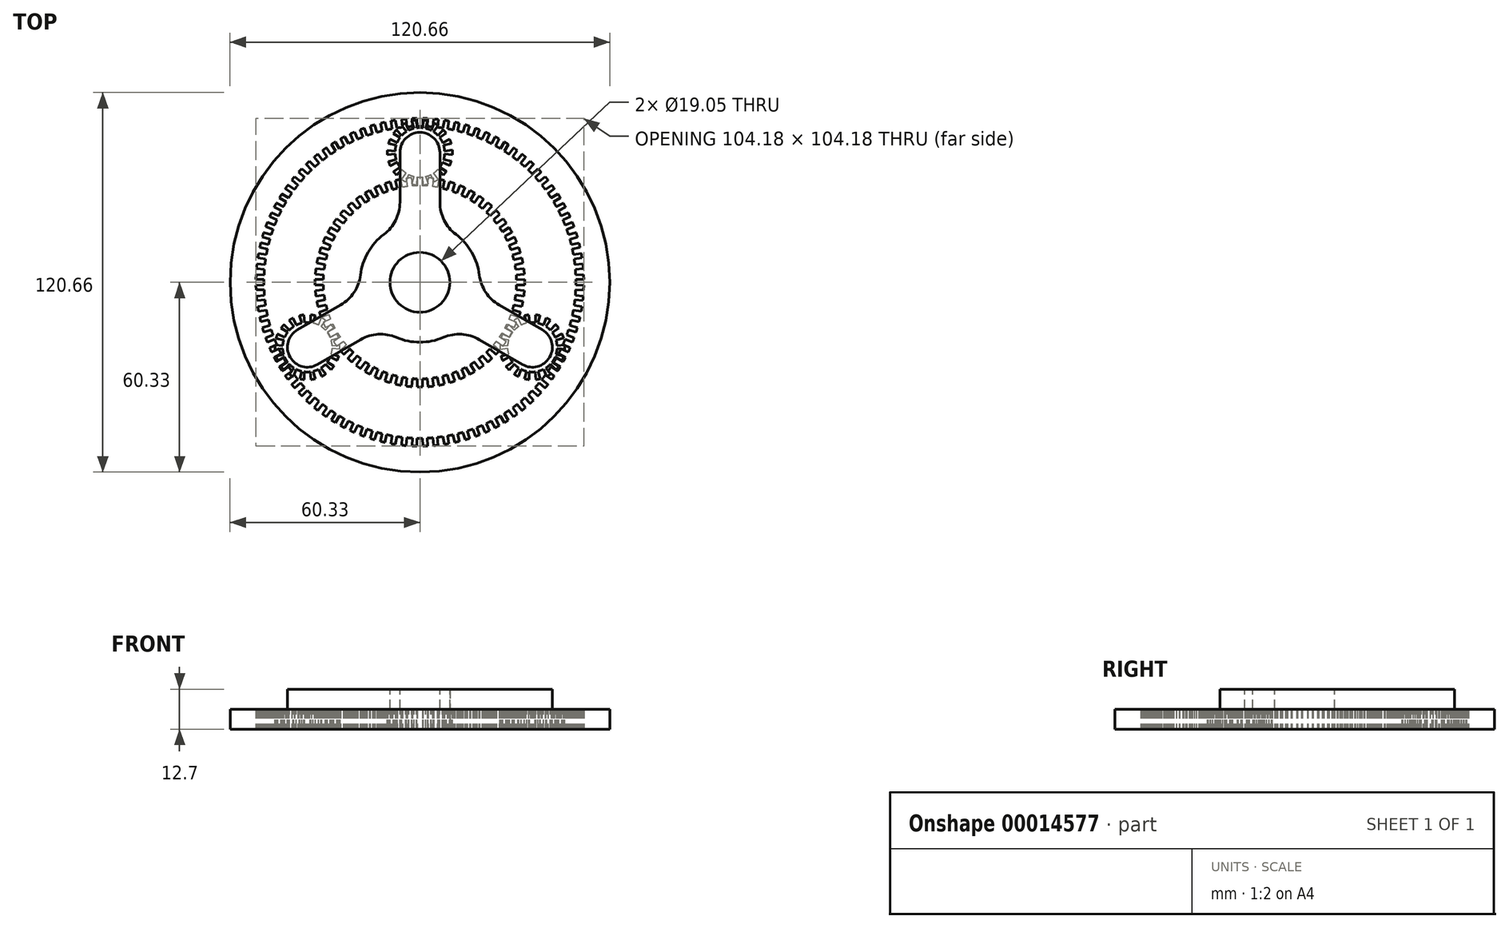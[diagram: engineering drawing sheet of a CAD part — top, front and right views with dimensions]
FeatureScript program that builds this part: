
annotation { "Feature Type Name" : "Feature", "Feature Type Description" : "" }
export const myFeature = defineFeature(function(context is Context, id is Id, definition is map)
    precondition{}
    {
        {
            var Q0;
            Q0=qCreatedBy(makeId("Top.planeOp"),FACE);
            var sketch = newSketch(context, id + "F0", { "sketchPlane" : qUnion([Q0])});
            skCircle(sketch, "E0", {"center": v(0, 0) * mm, "radius": 9.53 * mm});
            skCircle(sketch, "E1", {"center": v(0, 0) * mm, "radius": 31.75 * mm, "construction": true});
            skLineSegment(sketch, "E2", {"start": v(0.87, 30.7) * mm, "end": v(0.87, 33.3) * mm});
            skArc(sketch, "E3", {"start": v(0.87, 33.3) * mm, "mid": v(0, 33.3) * mm, "end": v(-0.87, 33.3) * mm});
            skLineSegment(sketch, "E4", {"start": v(-0.87, 33.3) * mm, "end": v(-0.83, 30.7) * mm});
            skArc(sketch, "E5", {"start": v(-0.83, 30.7) * mm, "mid": v(-1.59, 30.66) * mm, "end": v(-2.34, 30.61) * mm});
            skLineSegment(sketch, "E6", {"start": v(1.05, 36.8) * mm, "end": v(0, 0) * mm, "construction": true});
            skLineSegment(sketch, "E7", {"start": v(0, 0) * mm, "end": v(-2.79, 36.45) * mm, "construction": true});
            skLineSegment(sketch, "E8.1.0", {"start": v(-2.34, 30.61) * mm, "end": v(-2.61, 33.2) * mm});
            skArc(sketch, "E8.1.1", {"start": v(-2.61, 33.2) * mm, "mid": v(-3.48, 33.13) * mm, "end": v(-4.35, 33.02) * mm});
            skLineSegment(sketch, "E8.1.2", {"start": v(-4.35, 33.02) * mm, "end": v(-4.04, 30.44) * mm});
            skArc(sketch, "E8.1.3", {"start": v(-4.04, 30.44) * mm, "mid": v(-4.78, 30.33) * mm, "end": v(-5.53, 30.2) * mm});
            skLineSegment(sketch, "E8.2.0", {"start": v(-5.53, 30.2) * mm, "end": v(-6.07, 32.75) * mm});
            skArc(sketch, "E8.2.1", {"start": v(-6.07, 32.75) * mm, "mid": v(-6.93, 32.58) * mm, "end": v(-7.78, 32.39) * mm});
            skLineSegment(sketch, "E8.2.2", {"start": v(-7.78, 32.39) * mm, "end": v(-7.2, 29.85) * mm});
            skArc(sketch, "E8.2.3", {"start": v(-7.2, 29.85) * mm, "mid": v(-7.93, 29.66) * mm, "end": v(-8.65, 29.46) * mm});
            skLineSegment(sketch, "E8.3.0", {"start": v(-8.65, 29.46) * mm, "end": v(-9.46, 31.94) * mm});
            skArc(sketch, "E8.3.1", {"start": v(-9.46, 31.94) * mm, "mid": v(-10.3, 31.68) * mm, "end": v(-11.12, 31.4) * mm});
            skLineSegment(sketch, "E8.3.2", {"start": v(-11.12, 31.4) * mm, "end": v(-10.28, 28.93) * mm});
            skArc(sketch, "E8.3.3", {"start": v(-10.28, 28.93) * mm, "mid": v(-10.98, 28.67) * mm, "end": v(-11.69, 28.4) * mm});
            skLineSegment(sketch, "E8.4.0", {"start": v(-11.69, 28.4) * mm, "end": v(-12.75, 30.77) * mm});
            skArc(sketch, "E8.4.1", {"start": v(-12.75, 30.77) * mm, "mid": v(-13.55, 30.43) * mm, "end": v(-14.34, 30.06) * mm});
            skLineSegment(sketch, "E8.4.2", {"start": v(-14.34, 30.06) * mm, "end": v(-13.24, 27.7) * mm});
            skArc(sketch, "E8.4.3", {"start": v(-13.24, 27.7) * mm, "mid": v(-13.92, 27.37) * mm, "end": v(-14.59, 27.01) * mm});
            skLineSegment(sketch, "E8.5.0", {"start": v(-14.59, 27.01) * mm, "end": v(-15.9, 29.27) * mm});
            skArc(sketch, "E8.5.1", {"start": v(-15.9, 29.27) * mm, "mid": v(-16.65, 28.85) * mm, "end": v(-17.4, 28.4) * mm});
            skLineSegment(sketch, "E8.5.2", {"start": v(-17.4, 28.4) * mm, "end": v(-16.07, 26.16) * mm});
            skArc(sketch, "E8.5.3", {"start": v(-16.07, 26.16) * mm, "mid": v(-16.7, 25.76) * mm, "end": v(-17.33, 25.34) * mm});
            skLineSegment(sketch, "E8.6.0", {"start": v(-17.33, 25.34) * mm, "end": v(-18.87, 27.45) * mm});
            skArc(sketch, "E8.6.1", {"start": v(-18.87, 27.45) * mm, "mid": v(-19.58, 26.95) * mm, "end": v(-20.28, 26.42) * mm});
            skLineSegment(sketch, "E8.6.2", {"start": v(-20.28, 26.42) * mm, "end": v(-18.71, 24.34) * mm});
            skArc(sketch, "E8.6.3", {"start": v(-18.71, 24.34) * mm, "mid": v(-19.3, 23.87) * mm, "end": v(-19.89, 23.4) * mm});
            skLineSegment(sketch, "E8.7.0", {"start": v(-19.89, 23.4) * mm, "end": v(-21.63, 25.33) * mm});
            skArc(sketch, "E8.7.1", {"start": v(-21.63, 25.33) * mm, "mid": v(-22.29, 24.75) * mm, "end": v(-22.93, 24.16) * mm});
            skLineSegment(sketch, "E8.7.2", {"start": v(-22.93, 24.16) * mm, "end": v(-21.16, 22.25) * mm});
            skArc(sketch, "E8.7.3", {"start": v(-21.16, 22.25) * mm, "mid": v(-21.7, 21.72) * mm, "end": v(-22.22, 21.18) * mm});
            skLineSegment(sketch, "E8.8.0", {"start": v(-22.22, 21.18) * mm, "end": v(-24.16, 22.93) * mm});
            skArc(sketch, "E8.8.1", {"start": v(-24.16, 22.93) * mm, "mid": v(-24.75, 22.29) * mm, "end": v(-25.33, 21.63) * mm});
            skLineSegment(sketch, "E8.8.2", {"start": v(-25.33, 21.63) * mm, "end": v(-23.37, 19.92) * mm});
            skArc(sketch, "E8.8.3", {"start": v(-23.37, 19.92) * mm, "mid": v(-23.85, 19.34) * mm, "end": v(-24.32, 18.75) * mm});
            skLineSegment(sketch, "E8.9.0", {"start": v(-24.32, 18.75) * mm, "end": v(-26.42, 20.28) * mm});
            skArc(sketch, "E8.9.1", {"start": v(-26.42, 20.28) * mm, "mid": v(-26.95, 19.58) * mm, "end": v(-27.45, 18.87) * mm});
            skLineSegment(sketch, "E8.9.2", {"start": v(-27.45, 18.87) * mm, "end": v(-25.32, 17.37) * mm});
            skArc(sketch, "E8.9.3", {"start": v(-25.32, 17.37) * mm, "mid": v(-25.74, 16.74) * mm, "end": v(-26.14, 16.1) * mm});
            skLineSegment(sketch, "E8.10.0", {"start": v(-26.14, 16.1) * mm, "end": v(-28.4, 17.4) * mm});
            skArc(sketch, "E8.10.1", {"start": v(-28.4, 17.4) * mm, "mid": v(-28.85, 16.65) * mm, "end": v(-29.27, 15.9) * mm});
            skLineSegment(sketch, "E8.10.2", {"start": v(-29.27, 15.9) * mm, "end": v(-27, 14.62) * mm});
            skArc(sketch, "E8.10.3", {"start": v(-27, 14.62) * mm, "mid": v(-27.35, 13.96) * mm, "end": v(-27.68, 13.28) * mm});
            skLineSegment(sketch, "E8.11.0", {"start": v(-27.68, 13.28) * mm, "end": v(-30.06, 14.34) * mm});
            skArc(sketch, "E8.11.1", {"start": v(-30.06, 14.34) * mm, "mid": v(-30.43, 13.55) * mm, "end": v(-30.77, 12.75) * mm});
            skLineSegment(sketch, "E8.11.2", {"start": v(-30.77, 12.75) * mm, "end": v(-28.38, 11.72) * mm});
            skArc(sketch, "E8.11.3", {"start": v(-28.38, 11.72) * mm, "mid": v(-28.66, 11.02) * mm, "end": v(-28.92, 10.31) * mm});
            skLineSegment(sketch, "E8.12.0", {"start": v(-28.92, 10.31) * mm, "end": v(-31.4, 11.12) * mm});
            skArc(sketch, "E8.12.1", {"start": v(-31.4, 11.12) * mm, "mid": v(-31.68, 10.3) * mm, "end": v(-31.94, 9.46) * mm});
            skLineSegment(sketch, "E8.12.2", {"start": v(-31.94, 9.46) * mm, "end": v(-29.45, 8.7) * mm});
            skArc(sketch, "E8.12.3", {"start": v(-29.45, 8.7) * mm, "mid": v(-29.65, 7.97) * mm, "end": v(-29.84, 7.23) * mm});
            skLineSegment(sketch, "E8.13.0", {"start": v(-29.84, 7.23) * mm, "end": v(-32.39, 7.78) * mm});
            skArc(sketch, "E8.13.1", {"start": v(-32.39, 7.78) * mm, "mid": v(-32.58, 6.93) * mm, "end": v(-32.75, 6.07) * mm});
            skLineSegment(sketch, "E8.13.2", {"start": v(-32.75, 6.07) * mm, "end": v(-30.2, 5.57) * mm});
            skArc(sketch, "E8.13.3", {"start": v(-30.2, 5.57) * mm, "mid": v(-30.32, 4.82) * mm, "end": v(-30.43, 4.08) * mm});
            skLineSegment(sketch, "E8.14.0", {"start": v(-30.43, 4.08) * mm, "end": v(-33.02, 4.35) * mm});
            skArc(sketch, "E8.14.1", {"start": v(-33.02, 4.35) * mm, "mid": v(-33.13, 3.48) * mm, "end": v(-33.2, 2.61) * mm});
            skLineSegment(sketch, "E8.14.2", {"start": v(-33.2, 2.61) * mm, "end": v(-30.61, 2.38) * mm});
            skArc(sketch, "E8.14.3", {"start": v(-30.61, 2.38) * mm, "mid": v(-30.66, 1.63) * mm, "end": v(-30.7, 0.87) * mm});
            skLineSegment(sketch, "E8.15.0", {"start": v(-30.7, 0.87) * mm, "end": v(-33.3, 0.87) * mm});
            skArc(sketch, "E8.15.1", {"start": v(-33.3, 0.87) * mm, "mid": v(-33.3, 0) * mm, "end": v(-33.3, -0.87) * mm});
            skLineSegment(sketch, "E8.15.2", {"start": v(-33.3, -0.87) * mm, "end": v(-30.7, -0.83) * mm});
            skArc(sketch, "E8.15.3", {"start": v(-30.7, -0.83) * mm, "mid": v(-30.66, -1.59) * mm, "end": v(-30.61, -2.34) * mm});
            skLineSegment(sketch, "E8.16.0", {"start": v(-30.61, -2.34) * mm, "end": v(-33.2, -2.61) * mm});
            skArc(sketch, "E8.16.1", {"start": v(-33.2, -2.61) * mm, "mid": v(-33.13, -3.48) * mm, "end": v(-33.02, -4.35) * mm});
            skLineSegment(sketch, "E8.16.2", {"start": v(-33.02, -4.35) * mm, "end": v(-30.44, -4.04) * mm});
            skArc(sketch, "E8.16.3", {"start": v(-30.44, -4.04) * mm, "mid": v(-30.33, -4.78) * mm, "end": v(-30.2, -5.53) * mm});
            skLineSegment(sketch, "E8.17.0", {"start": v(-30.2, -5.53) * mm, "end": v(-32.75, -6.07) * mm});
            skArc(sketch, "E8.17.1", {"start": v(-32.75, -6.07) * mm, "mid": v(-32.58, -6.93) * mm, "end": v(-32.39, -7.78) * mm});
            skLineSegment(sketch, "E8.17.2", {"start": v(-32.39, -7.78) * mm, "end": v(-29.85, -7.2) * mm});
            skArc(sketch, "E8.17.3", {"start": v(-29.85, -7.2) * mm, "mid": v(-29.66, -7.93) * mm, "end": v(-29.46, -8.65) * mm});
            skLineSegment(sketch, "E8.18.0", {"start": v(-29.46, -8.65) * mm, "end": v(-31.94, -9.46) * mm});
            skArc(sketch, "E8.18.1", {"start": v(-31.94, -9.46) * mm, "mid": v(-31.68, -10.3) * mm, "end": v(-31.4, -11.12) * mm});
            skLineSegment(sketch, "E8.18.2", {"start": v(-31.4, -11.12) * mm, "end": v(-28.93, -10.28) * mm});
            skArc(sketch, "E8.18.3", {"start": v(-28.93, -10.28) * mm, "mid": v(-28.67, -10.98) * mm, "end": v(-28.4, -11.69) * mm});
            skLineSegment(sketch, "E8.19.0", {"start": v(-28.4, -11.69) * mm, "end": v(-30.77, -12.75) * mm});
            skArc(sketch, "E8.19.1", {"start": v(-30.77, -12.75) * mm, "mid": v(-30.43, -13.55) * mm, "end": v(-30.06, -14.34) * mm});
            skLineSegment(sketch, "E8.19.2", {"start": v(-30.06, -14.34) * mm, "end": v(-27.7, -13.24) * mm});
            skArc(sketch, "E8.19.3", {"start": v(-27.7, -13.24) * mm, "mid": v(-27.37, -13.92) * mm, "end": v(-27.01, -14.59) * mm});
            skLineSegment(sketch, "E8.20.0", {"start": v(-27.01, -14.59) * mm, "end": v(-29.27, -15.9) * mm});
            skArc(sketch, "E8.20.1", {"start": v(-29.27, -15.9) * mm, "mid": v(-28.85, -16.65) * mm, "end": v(-28.4, -17.4) * mm});
            skLineSegment(sketch, "E8.20.2", {"start": v(-28.4, -17.4) * mm, "end": v(-26.16, -16.07) * mm});
            skArc(sketch, "E8.20.3", {"start": v(-26.16, -16.07) * mm, "mid": v(-25.76, -16.7) * mm, "end": v(-25.34, -17.33) * mm});
            skLineSegment(sketch, "E8.21.0", {"start": v(-25.34, -17.33) * mm, "end": v(-27.45, -18.87) * mm});
            skArc(sketch, "E8.21.1", {"start": v(-27.45, -18.87) * mm, "mid": v(-26.95, -19.58) * mm, "end": v(-26.42, -20.28) * mm});
            skLineSegment(sketch, "E8.21.2", {"start": v(-26.42, -20.28) * mm, "end": v(-24.34, -18.71) * mm});
            skArc(sketch, "E8.21.3", {"start": v(-24.34, -18.71) * mm, "mid": v(-23.87, -19.3) * mm, "end": v(-23.4, -19.89) * mm});
            skLineSegment(sketch, "E8.22.0", {"start": v(-23.4, -19.89) * mm, "end": v(-25.33, -21.63) * mm});
            skArc(sketch, "E8.22.1", {"start": v(-25.33, -21.63) * mm, "mid": v(-24.75, -22.29) * mm, "end": v(-24.16, -22.93) * mm});
            skLineSegment(sketch, "E8.22.2", {"start": v(-24.16, -22.93) * mm, "end": v(-22.25, -21.16) * mm});
            skArc(sketch, "E8.22.3", {"start": v(-22.25, -21.16) * mm, "mid": v(-21.72, -21.7) * mm, "end": v(-21.18, -22.22) * mm});
            skLineSegment(sketch, "E8.23.0", {"start": v(-21.18, -22.22) * mm, "end": v(-22.93, -24.16) * mm});
            skArc(sketch, "E8.23.1", {"start": v(-22.93, -24.16) * mm, "mid": v(-22.29, -24.75) * mm, "end": v(-21.63, -25.33) * mm});
            skLineSegment(sketch, "E8.23.2", {"start": v(-21.63, -25.33) * mm, "end": v(-19.92, -23.37) * mm});
            skArc(sketch, "E8.23.3", {"start": v(-19.92, -23.37) * mm, "mid": v(-19.34, -23.85) * mm, "end": v(-18.75, -24.32) * mm});
            skLineSegment(sketch, "E8.24.0", {"start": v(-18.75, -24.32) * mm, "end": v(-20.28, -26.42) * mm});
            skArc(sketch, "E8.24.1", {"start": v(-20.28, -26.42) * mm, "mid": v(-19.58, -26.95) * mm, "end": v(-18.87, -27.45) * mm});
            skLineSegment(sketch, "E8.24.2", {"start": v(-18.87, -27.45) * mm, "end": v(-17.37, -25.32) * mm});
            skArc(sketch, "E8.24.3", {"start": v(-17.37, -25.32) * mm, "mid": v(-16.74, -25.74) * mm, "end": v(-16.1, -26.14) * mm});
            skLineSegment(sketch, "E8.25.0", {"start": v(-16.1, -26.14) * mm, "end": v(-17.4, -28.4) * mm});
            skArc(sketch, "E8.25.1", {"start": v(-17.4, -28.4) * mm, "mid": v(-16.65, -28.85) * mm, "end": v(-15.9, -29.27) * mm});
            skLineSegment(sketch, "E8.25.2", {"start": v(-15.9, -29.27) * mm, "end": v(-14.62, -27) * mm});
            skArc(sketch, "E8.25.3", {"start": v(-14.62, -27) * mm, "mid": v(-13.96, -27.35) * mm, "end": v(-13.28, -27.68) * mm});
            skLineSegment(sketch, "E8.26.0", {"start": v(-13.28, -27.68) * mm, "end": v(-14.34, -30.06) * mm});
            skArc(sketch, "E8.26.1", {"start": v(-14.34, -30.06) * mm, "mid": v(-13.55, -30.43) * mm, "end": v(-12.75, -30.77) * mm});
            skLineSegment(sketch, "E8.26.2", {"start": v(-12.75, -30.77) * mm, "end": v(-11.72, -28.38) * mm});
            skArc(sketch, "E8.26.3", {"start": v(-11.72, -28.38) * mm, "mid": v(-11.02, -28.66) * mm, "end": v(-10.31, -28.92) * mm});
            skLineSegment(sketch, "E8.27.0", {"start": v(-10.31, -28.92) * mm, "end": v(-11.12, -31.4) * mm});
            skArc(sketch, "E8.27.1", {"start": v(-11.12, -31.4) * mm, "mid": v(-10.3, -31.68) * mm, "end": v(-9.46, -31.94) * mm});
            skLineSegment(sketch, "E8.27.2", {"start": v(-9.46, -31.94) * mm, "end": v(-8.7, -29.45) * mm});
            skArc(sketch, "E8.27.3", {"start": v(-8.7, -29.45) * mm, "mid": v(-7.97, -29.65) * mm, "end": v(-7.23, -29.84) * mm});
            skLineSegment(sketch, "E8.28.0", {"start": v(-7.23, -29.84) * mm, "end": v(-7.78, -32.39) * mm});
            skArc(sketch, "E8.28.1", {"start": v(-7.78, -32.39) * mm, "mid": v(-6.93, -32.58) * mm, "end": v(-6.07, -32.75) * mm});
            skLineSegment(sketch, "E8.28.2", {"start": v(-6.07, -32.75) * mm, "end": v(-5.57, -30.2) * mm});
            skArc(sketch, "E8.28.3", {"start": v(-5.57, -30.2) * mm, "mid": v(-4.82, -30.32) * mm, "end": v(-4.08, -30.43) * mm});
            skLineSegment(sketch, "E8.29.0", {"start": v(-4.08, -30.43) * mm, "end": v(-4.35, -33.02) * mm});
            skArc(sketch, "E8.29.1", {"start": v(-4.35, -33.02) * mm, "mid": v(-3.48, -33.13) * mm, "end": v(-2.61, -33.2) * mm});
            skLineSegment(sketch, "E8.29.2", {"start": v(-2.61, -33.2) * mm, "end": v(-2.38, -30.61) * mm});
            skArc(sketch, "E8.29.3", {"start": v(-2.38, -30.61) * mm, "mid": v(-1.63, -30.66) * mm, "end": v(-0.87, -30.7) * mm});
            skLineSegment(sketch, "E8.30.0", {"start": v(-0.87, -30.7) * mm, "end": v(-0.87, -33.3) * mm});
            skArc(sketch, "E8.30.1", {"start": v(-0.87, -33.3) * mm, "mid": v(0, -33.3) * mm, "end": v(0.87, -33.3) * mm});
            skLineSegment(sketch, "E8.30.2", {"start": v(0.87, -33.3) * mm, "end": v(0.83, -30.7) * mm});
            skArc(sketch, "E8.30.3", {"start": v(0.83, -30.7) * mm, "mid": v(1.59, -30.66) * mm, "end": v(2.34, -30.61) * mm});
            skLineSegment(sketch, "E8.31.0", {"start": v(2.34, -30.61) * mm, "end": v(2.61, -33.2) * mm});
            skArc(sketch, "E8.31.1", {"start": v(2.61, -33.2) * mm, "mid": v(3.48, -33.13) * mm, "end": v(4.35, -33.02) * mm});
            skLineSegment(sketch, "E8.31.2", {"start": v(4.35, -33.02) * mm, "end": v(4.04, -30.44) * mm});
            skArc(sketch, "E8.31.3", {"start": v(4.04, -30.44) * mm, "mid": v(4.78, -30.33) * mm, "end": v(5.53, -30.2) * mm});
            skLineSegment(sketch, "E8.32.0", {"start": v(5.53, -30.2) * mm, "end": v(6.07, -32.75) * mm});
            skArc(sketch, "E8.32.1", {"start": v(6.07, -32.75) * mm, "mid": v(6.93, -32.58) * mm, "end": v(7.78, -32.39) * mm});
            skLineSegment(sketch, "E8.32.2", {"start": v(7.78, -32.39) * mm, "end": v(7.2, -29.85) * mm});
            skArc(sketch, "E8.32.3", {"start": v(7.2, -29.85) * mm, "mid": v(7.93, -29.66) * mm, "end": v(8.65, -29.46) * mm});
            skLineSegment(sketch, "E8.33.0", {"start": v(8.65, -29.46) * mm, "end": v(9.46, -31.94) * mm});
            skArc(sketch, "E8.33.1", {"start": v(9.46, -31.94) * mm, "mid": v(10.3, -31.68) * mm, "end": v(11.12, -31.4) * mm});
            skLineSegment(sketch, "E8.33.2", {"start": v(11.12, -31.4) * mm, "end": v(10.28, -28.93) * mm});
            skArc(sketch, "E8.33.3", {"start": v(10.28, -28.93) * mm, "mid": v(10.98, -28.67) * mm, "end": v(11.69, -28.4) * mm});
            skLineSegment(sketch, "E8.34.0", {"start": v(11.69, -28.4) * mm, "end": v(12.75, -30.77) * mm});
            skArc(sketch, "E8.34.1", {"start": v(12.75, -30.77) * mm, "mid": v(13.55, -30.43) * mm, "end": v(14.34, -30.06) * mm});
            skLineSegment(sketch, "E8.34.2", {"start": v(14.34, -30.06) * mm, "end": v(13.24, -27.7) * mm});
            skArc(sketch, "E8.34.3", {"start": v(13.24, -27.7) * mm, "mid": v(13.92, -27.37) * mm, "end": v(14.59, -27.01) * mm});
            skLineSegment(sketch, "E8.35.0", {"start": v(14.59, -27.01) * mm, "end": v(15.9, -29.27) * mm});
            skArc(sketch, "E8.35.1", {"start": v(15.9, -29.27) * mm, "mid": v(16.65, -28.85) * mm, "end": v(17.4, -28.4) * mm});
            skLineSegment(sketch, "E8.35.2", {"start": v(17.4, -28.4) * mm, "end": v(16.07, -26.16) * mm});
            skArc(sketch, "E8.35.3", {"start": v(16.07, -26.16) * mm, "mid": v(16.7, -25.76) * mm, "end": v(17.33, -25.34) * mm});
            skLineSegment(sketch, "E8.36.0", {"start": v(17.33, -25.34) * mm, "end": v(18.87, -27.45) * mm});
            skArc(sketch, "E8.36.1", {"start": v(18.87, -27.45) * mm, "mid": v(19.58, -26.95) * mm, "end": v(20.28, -26.42) * mm});
            skLineSegment(sketch, "E8.36.2", {"start": v(20.28, -26.42) * mm, "end": v(18.71, -24.34) * mm});
            skArc(sketch, "E8.36.3", {"start": v(18.71, -24.34) * mm, "mid": v(19.3, -23.87) * mm, "end": v(19.89, -23.4) * mm});
            skLineSegment(sketch, "E8.37.0", {"start": v(19.89, -23.4) * mm, "end": v(21.63, -25.33) * mm});
            skArc(sketch, "E8.37.1", {"start": v(21.63, -25.33) * mm, "mid": v(22.29, -24.75) * mm, "end": v(22.93, -24.16) * mm});
            skLineSegment(sketch, "E8.37.2", {"start": v(22.93, -24.16) * mm, "end": v(21.16, -22.25) * mm});
            skArc(sketch, "E8.37.3", {"start": v(21.16, -22.25) * mm, "mid": v(21.7, -21.72) * mm, "end": v(22.22, -21.18) * mm});
            skLineSegment(sketch, "E8.38.0", {"start": v(22.22, -21.18) * mm, "end": v(24.16, -22.93) * mm});
            skArc(sketch, "E8.38.1", {"start": v(24.16, -22.93) * mm, "mid": v(24.75, -22.29) * mm, "end": v(25.33, -21.63) * mm});
            skLineSegment(sketch, "E8.38.2", {"start": v(25.33, -21.63) * mm, "end": v(23.37, -19.92) * mm});
            skArc(sketch, "E8.38.3", {"start": v(23.37, -19.92) * mm, "mid": v(23.85, -19.34) * mm, "end": v(24.32, -18.75) * mm});
            skLineSegment(sketch, "E8.39.0", {"start": v(24.32, -18.75) * mm, "end": v(26.42, -20.28) * mm});
            skArc(sketch, "E8.39.1", {"start": v(26.42, -20.28) * mm, "mid": v(26.95, -19.58) * mm, "end": v(27.45, -18.87) * mm});
            skLineSegment(sketch, "E8.39.2", {"start": v(27.45, -18.87) * mm, "end": v(25.32, -17.37) * mm});
            skArc(sketch, "E8.39.3", {"start": v(25.32, -17.37) * mm, "mid": v(25.74, -16.74) * mm, "end": v(26.14, -16.1) * mm});
            skLineSegment(sketch, "E8.40.0", {"start": v(26.14, -16.1) * mm, "end": v(28.4, -17.4) * mm});
            skArc(sketch, "E8.40.1", {"start": v(28.4, -17.4) * mm, "mid": v(28.85, -16.65) * mm, "end": v(29.27, -15.9) * mm});
            skLineSegment(sketch, "E8.40.2", {"start": v(29.27, -15.9) * mm, "end": v(27, -14.62) * mm});
            skArc(sketch, "E8.40.3", {"start": v(27, -14.62) * mm, "mid": v(27.35, -13.96) * mm, "end": v(27.68, -13.28) * mm});
            skLineSegment(sketch, "E8.41.0", {"start": v(27.68, -13.28) * mm, "end": v(30.06, -14.34) * mm});
            skArc(sketch, "E8.41.1", {"start": v(30.06, -14.34) * mm, "mid": v(30.43, -13.55) * mm, "end": v(30.77, -12.75) * mm});
            skLineSegment(sketch, "E8.41.2", {"start": v(30.77, -12.75) * mm, "end": v(28.38, -11.72) * mm});
            skArc(sketch, "E8.41.3", {"start": v(28.38, -11.72) * mm, "mid": v(28.66, -11.02) * mm, "end": v(28.92, -10.31) * mm});
            skLineSegment(sketch, "E8.42.0", {"start": v(28.92, -10.31) * mm, "end": v(31.4, -11.12) * mm});
            skArc(sketch, "E8.42.1", {"start": v(31.4, -11.12) * mm, "mid": v(31.68, -10.3) * mm, "end": v(31.94, -9.46) * mm});
            skLineSegment(sketch, "E8.42.2", {"start": v(31.94, -9.46) * mm, "end": v(29.45, -8.7) * mm});
            skArc(sketch, "E8.42.3", {"start": v(29.45, -8.7) * mm, "mid": v(29.65, -7.97) * mm, "end": v(29.84, -7.23) * mm});
            skLineSegment(sketch, "E8.43.0", {"start": v(29.84, -7.23) * mm, "end": v(32.39, -7.78) * mm});
            skArc(sketch, "E8.43.1", {"start": v(32.39, -7.78) * mm, "mid": v(32.58, -6.93) * mm, "end": v(32.75, -6.07) * mm});
            skLineSegment(sketch, "E8.43.2", {"start": v(32.75, -6.07) * mm, "end": v(30.2, -5.57) * mm});
            skArc(sketch, "E8.43.3", {"start": v(30.2, -5.57) * mm, "mid": v(30.32, -4.82) * mm, "end": v(30.43, -4.08) * mm});
            skLineSegment(sketch, "E8.44.0", {"start": v(30.43, -4.08) * mm, "end": v(33.02, -4.35) * mm});
            skArc(sketch, "E8.44.1", {"start": v(33.02, -4.35) * mm, "mid": v(33.13, -3.48) * mm, "end": v(33.2, -2.61) * mm});
            skLineSegment(sketch, "E8.44.2", {"start": v(33.2, -2.61) * mm, "end": v(30.61, -2.38) * mm});
            skArc(sketch, "E8.44.3", {"start": v(30.61, -2.38) * mm, "mid": v(30.66, -1.63) * mm, "end": v(30.7, -0.87) * mm});
            skLineSegment(sketch, "E8.45.0", {"start": v(30.7, -0.87) * mm, "end": v(33.3, -0.87) * mm});
            skArc(sketch, "E8.45.1", {"start": v(33.3, -0.87) * mm, "mid": v(33.3, 0) * mm, "end": v(33.3, 0.87) * mm});
            skLineSegment(sketch, "E8.45.2", {"start": v(33.3, 0.87) * mm, "end": v(30.7, 0.83) * mm});
            skArc(sketch, "E8.45.3", {"start": v(30.7, 0.83) * mm, "mid": v(30.66, 1.59) * mm, "end": v(30.61, 2.34) * mm});
            skLineSegment(sketch, "E8.46.0", {"start": v(30.61, 2.34) * mm, "end": v(33.2, 2.61) * mm});
            skArc(sketch, "E8.46.1", {"start": v(33.2, 2.61) * mm, "mid": v(33.13, 3.48) * mm, "end": v(33.02, 4.35) * mm});
            skLineSegment(sketch, "E8.46.2", {"start": v(33.02, 4.35) * mm, "end": v(30.44, 4.04) * mm});
            skArc(sketch, "E8.46.3", {"start": v(30.44, 4.04) * mm, "mid": v(30.33, 4.78) * mm, "end": v(30.2, 5.53) * mm});
            skLineSegment(sketch, "E8.47.0", {"start": v(30.2, 5.53) * mm, "end": v(32.75, 6.07) * mm});
            skArc(sketch, "E8.47.1", {"start": v(32.75, 6.07) * mm, "mid": v(32.58, 6.93) * mm, "end": v(32.39, 7.78) * mm});
            skLineSegment(sketch, "E8.47.2", {"start": v(32.39, 7.78) * mm, "end": v(29.85, 7.2) * mm});
            skArc(sketch, "E8.47.3", {"start": v(29.85, 7.2) * mm, "mid": v(29.66, 7.93) * mm, "end": v(29.46, 8.65) * mm});
            skLineSegment(sketch, "E8.48.0", {"start": v(29.46, 8.65) * mm, "end": v(31.94, 9.46) * mm});
            skArc(sketch, "E8.48.1", {"start": v(31.94, 9.46) * mm, "mid": v(31.68, 10.3) * mm, "end": v(31.4, 11.12) * mm});
            skLineSegment(sketch, "E8.48.2", {"start": v(31.4, 11.12) * mm, "end": v(28.93, 10.28) * mm});
            skArc(sketch, "E8.48.3", {"start": v(28.93, 10.28) * mm, "mid": v(28.67, 10.98) * mm, "end": v(28.4, 11.69) * mm});
            skLineSegment(sketch, "E8.49.0", {"start": v(28.4, 11.69) * mm, "end": v(30.77, 12.75) * mm});
            skArc(sketch, "E8.49.1", {"start": v(30.77, 12.75) * mm, "mid": v(30.43, 13.55) * mm, "end": v(30.06, 14.34) * mm});
            skLineSegment(sketch, "E8.49.2", {"start": v(30.06, 14.34) * mm, "end": v(27.7, 13.24) * mm});
            skArc(sketch, "E8.49.3", {"start": v(27.7, 13.24) * mm, "mid": v(27.37, 13.92) * mm, "end": v(27.01, 14.59) * mm});
            skLineSegment(sketch, "E8.50.0", {"start": v(27.01, 14.59) * mm, "end": v(29.27, 15.9) * mm});
            skArc(sketch, "E8.50.1", {"start": v(29.27, 15.9) * mm, "mid": v(28.85, 16.65) * mm, "end": v(28.4, 17.4) * mm});
            skLineSegment(sketch, "E8.50.2", {"start": v(28.4, 17.4) * mm, "end": v(26.16, 16.07) * mm});
            skArc(sketch, "E8.50.3", {"start": v(26.16, 16.07) * mm, "mid": v(25.76, 16.7) * mm, "end": v(25.34, 17.33) * mm});
            skLineSegment(sketch, "E8.51.0", {"start": v(25.34, 17.33) * mm, "end": v(27.45, 18.87) * mm});
            skArc(sketch, "E8.51.1", {"start": v(27.45, 18.87) * mm, "mid": v(26.95, 19.58) * mm, "end": v(26.42, 20.28) * mm});
            skLineSegment(sketch, "E8.51.2", {"start": v(26.42, 20.28) * mm, "end": v(24.34, 18.71) * mm});
            skArc(sketch, "E8.51.3", {"start": v(24.34, 18.71) * mm, "mid": v(23.87, 19.3) * mm, "end": v(23.4, 19.89) * mm});
            skLineSegment(sketch, "E8.52.0", {"start": v(23.4, 19.89) * mm, "end": v(25.33, 21.63) * mm});
            skArc(sketch, "E8.52.1", {"start": v(25.33, 21.63) * mm, "mid": v(24.75, 22.29) * mm, "end": v(24.16, 22.93) * mm});
            skLineSegment(sketch, "E8.52.2", {"start": v(24.16, 22.93) * mm, "end": v(22.25, 21.16) * mm});
            skArc(sketch, "E8.52.3", {"start": v(22.25, 21.16) * mm, "mid": v(21.72, 21.7) * mm, "end": v(21.18, 22.22) * mm});
            skLineSegment(sketch, "E8.53.0", {"start": v(21.18, 22.22) * mm, "end": v(22.93, 24.16) * mm});
            skArc(sketch, "E8.53.1", {"start": v(22.93, 24.16) * mm, "mid": v(22.29, 24.75) * mm, "end": v(21.63, 25.33) * mm});
            skLineSegment(sketch, "E8.53.2", {"start": v(21.63, 25.33) * mm, "end": v(19.92, 23.37) * mm});
            skArc(sketch, "E8.53.3", {"start": v(19.92, 23.37) * mm, "mid": v(19.34, 23.85) * mm, "end": v(18.75, 24.32) * mm});
            skLineSegment(sketch, "E8.54.0", {"start": v(18.75, 24.32) * mm, "end": v(20.28, 26.42) * mm});
            skArc(sketch, "E8.54.1", {"start": v(20.28, 26.42) * mm, "mid": v(19.58, 26.95) * mm, "end": v(18.87, 27.45) * mm});
            skLineSegment(sketch, "E8.54.2", {"start": v(18.87, 27.45) * mm, "end": v(17.37, 25.32) * mm});
            skArc(sketch, "E8.54.3", {"start": v(17.37, 25.32) * mm, "mid": v(16.74, 25.74) * mm, "end": v(16.1, 26.14) * mm});
            skLineSegment(sketch, "E8.55.0", {"start": v(16.1, 26.14) * mm, "end": v(17.4, 28.4) * mm});
            skArc(sketch, "E8.55.1", {"start": v(17.4, 28.4) * mm, "mid": v(16.65, 28.85) * mm, "end": v(15.9, 29.27) * mm});
            skLineSegment(sketch, "E8.55.2", {"start": v(15.9, 29.27) * mm, "end": v(14.62, 27) * mm});
            skArc(sketch, "E8.55.3", {"start": v(14.62, 27) * mm, "mid": v(13.96, 27.35) * mm, "end": v(13.28, 27.68) * mm});
            skLineSegment(sketch, "E8.56.0", {"start": v(13.28, 27.68) * mm, "end": v(14.34, 30.06) * mm});
            skArc(sketch, "E8.56.1", {"start": v(14.34, 30.06) * mm, "mid": v(13.55, 30.43) * mm, "end": v(12.75, 30.77) * mm});
            skLineSegment(sketch, "E8.56.2", {"start": v(12.75, 30.77) * mm, "end": v(11.72, 28.38) * mm});
            skArc(sketch, "E8.56.3", {"start": v(11.72, 28.38) * mm, "mid": v(11.02, 28.66) * mm, "end": v(10.31, 28.92) * mm});
            skLineSegment(sketch, "E8.57.0", {"start": v(10.31, 28.92) * mm, "end": v(11.12, 31.4) * mm});
            skArc(sketch, "E8.57.1", {"start": v(11.12, 31.4) * mm, "mid": v(10.3, 31.68) * mm, "end": v(9.46, 31.94) * mm});
            skLineSegment(sketch, "E8.57.2", {"start": v(9.46, 31.94) * mm, "end": v(8.7, 29.45) * mm});
            skArc(sketch, "E8.57.3", {"start": v(8.7, 29.45) * mm, "mid": v(7.97, 29.65) * mm, "end": v(7.23, 29.84) * mm});
            skLineSegment(sketch, "E8.58.0", {"start": v(7.23, 29.84) * mm, "end": v(7.78, 32.39) * mm});
            skArc(sketch, "E8.58.1", {"start": v(7.78, 32.39) * mm, "mid": v(6.93, 32.58) * mm, "end": v(6.07, 32.75) * mm});
            skLineSegment(sketch, "E8.58.2", {"start": v(6.07, 32.75) * mm, "end": v(5.57, 30.2) * mm});
            skArc(sketch, "E8.58.3", {"start": v(5.57, 30.2) * mm, "mid": v(4.82, 30.32) * mm, "end": v(4.08, 30.43) * mm});
            skLineSegment(sketch, "E8.59.0", {"start": v(4.08, 30.43) * mm, "end": v(4.35, 33.02) * mm});
            skArc(sketch, "E8.59.1", {"start": v(4.35, 33.02) * mm, "mid": v(3.48, 33.13) * mm, "end": v(2.61, 33.2) * mm});
            skLineSegment(sketch, "E8.59.2", {"start": v(2.61, 33.2) * mm, "end": v(2.38, 30.61) * mm});
            skArc(sketch, "E8.59.3", {"start": v(2.38, 30.61) * mm, "mid": v(1.63, 30.66) * mm, "end": v(0.87, 30.7) * mm});
            skSolve(sketch);
        }
        {
            var Q0;
            Q0 = qSketchRegion(id + "F0", true);
            extrude(context, id + "F1", {"entities" : qUnion([Q0]), "depth" : 6.35 * mm});
        }
        {
            var Q0;
            Q0=makeQuery(id+"F0.imprint","IMPRINT",FACE,{"disambiguationData":[TD([[makeQuery(id+"F0.imprint","IMPRINT",EDGE,{"derivedFrom":sQuery(id+"F0.wireOp",EDGE,"E0")}),1.0]])]});
            extrude(context, id + "F2", {"entities" : qUnion([Q0]), "depth" : 12.7 * mm});
        }
        {
            var Q0;
            Q0=qCreatedBy(makeId("Top.planeOp"),FACE);
            var sketch = newSketch(context, id + "F3", { "sketchPlane" : qUnion([Q0])});
            skCircle(sketch, "E9", {"center": v(0, 0) * mm, "radius": 50.8 * mm, "construction": true});
            skCircle(sketch, "E10", {"center": v(0, 0) * mm, "radius": 60.33 * mm});
            skLineSegment(sketch, "E11", {"start": v(0, 0) * mm, "end": v(1.78, 54.22) * mm, "construction": true});
            skLineSegment(sketch, "E12", {"start": v(0, 0) * mm, "end": v(-1.75, 53.37) * mm, "construction": true});
            skLineSegment(sketch, "E13", {"start": v(0, 0) * mm, "end": v(0, 48.84) * mm, "construction": true});
            skArc(sketch, "E14", {"start": v(0.9, 49.58) * mm, "mid": v(0, 49.59) * mm, "end": v(-0.88, 49.58) * mm});
            skLineSegment(sketch, "E15", {"start": v(0.9, 49.58) * mm, "end": v(0.98, 52.09) * mm});
            skLineSegment(sketch, "E16", {"start": v(-0.88, 49.58) * mm, "end": v(-0.96, 52.09) * mm});
            skArc(sketch, "E17", {"start": v(-0.96, 52.09) * mm, "mid": v(-1.33, 52.08) * mm, "end": v(-1.7, 52.07) * mm});
            skArc(sketch, "E18.trimOffspring", {"start": v(1.7, 52.07) * mm, "mid": v(1.34, 52.08) * mm, "end": v(0.98, 52.09) * mm});
            skArc(sketch, "E19.1.0", {"start": v(-1.7, 52.07) * mm, "mid": v(-2.07, 52.06) * mm, "end": v(-2.43, 52.04) * mm});
            skLineSegment(sketch, "E19.1.1", {"start": v(-2.35, 49.53) * mm, "end": v(-2.43, 52.04) * mm});
            skArc(sketch, "E19.1.2", {"start": v(-2.35, 49.53) * mm, "mid": v(-3.24, 49.48) * mm, "end": v(-4.12, 49.42) * mm});
            skLineSegment(sketch, "E19.1.3", {"start": v(-4.12, 49.42) * mm, "end": v(-4.37, 51.91) * mm});
            skArc(sketch, "E19.1.4", {"start": v(-4.37, 51.91) * mm, "mid": v(-4.74, 51.88) * mm, "end": v(-5.1, 51.85) * mm});
            skArc(sketch, "E19.2.0", {"start": v(-5.1, 51.85) * mm, "mid": v(-5.47, 51.8) * mm, "end": v(-5.83, 51.77) * mm});
            skLineSegment(sketch, "E19.2.1", {"start": v(-5.58, 49.27) * mm, "end": v(-5.83, 51.77) * mm});
            skArc(sketch, "E19.2.2", {"start": v(-5.58, 49.27) * mm, "mid": v(-6.46, 49.17) * mm, "end": v(-7.34, 49.04) * mm});
            skLineSegment(sketch, "E19.2.3", {"start": v(-7.34, 49.04) * mm, "end": v(-7.75, 51.52) * mm});
            skArc(sketch, "E19.2.4", {"start": v(-7.75, 51.52) * mm, "mid": v(-8.12, 51.46) * mm, "end": v(-8.49, 51.4) * mm});
            skArc(sketch, "E20.1.3.0", {"start": v(-8.49, 51.4) * mm, "mid": v(-8.84, 51.34) * mm, "end": v(-9.2, 51.28) * mm});
            skLineSegment(sketch, "E20.4.3.0", {"start": v(-8.8, 48.8) * mm, "end": v(-9.2, 51.28) * mm});
            skArc(sketch, "E20.7.3.0", {"start": v(-8.8, 48.8) * mm, "mid": v(-9.67, 48.64) * mm, "end": v(-10.54, 48.46) * mm});
            skLineSegment(sketch, "E20.11.3.0", {"start": v(-10.54, 48.46) * mm, "end": v(-11.1, 50.9) * mm});
            skArc(sketch, "E20.14.3.0", {"start": v(-11.1, 50.9) * mm, "mid": v(-11.47, 50.82) * mm, "end": v(-11.83, 50.74) * mm});
            skArc(sketch, "E20.1.4.0", {"start": v(-11.83, 50.74) * mm, "mid": v(-12.18, 50.65) * mm, "end": v(-12.54, 50.57) * mm});
            skLineSegment(sketch, "E20.4.4.0", {"start": v(-11.97, 48.12) * mm, "end": v(-12.54, 50.57) * mm});
            skArc(sketch, "E20.7.4.0", {"start": v(-11.97, 48.12) * mm, "mid": v(-12.83, 47.9) * mm, "end": v(-13.68, 47.66) * mm});
            skLineSegment(sketch, "E20.11.4.0", {"start": v(-13.68, 47.66) * mm, "end": v(-14.41, 50.06) * mm});
            skArc(sketch, "E20.14.4.0", {"start": v(-14.41, 50.06) * mm, "mid": v(-14.77, 49.96) * mm, "end": v(-15.12, 49.85) * mm});
            skArc(sketch, "E20.1.5.0", {"start": v(-15.12, 49.85) * mm, "mid": v(-15.47, 49.75) * mm, "end": v(-15.82, 49.64) * mm});
            skLineSegment(sketch, "E20.4.5.0", {"start": v(-15.09, 47.24) * mm, "end": v(-15.82, 49.64) * mm});
            skArc(sketch, "E20.7.5.0", {"start": v(-15.09, 47.24) * mm, "mid": v(-15.93, 46.96) * mm, "end": v(-16.77, 46.67) * mm});
            skLineSegment(sketch, "E20.11.5.0", {"start": v(-16.77, 46.67) * mm, "end": v(-17.65, 49.01) * mm});
            skArc(sketch, "E20.14.5.0", {"start": v(-17.65, 49.01) * mm, "mid": v(-18, 48.89) * mm, "end": v(-18.35, 48.76) * mm});
            skArc(sketch, "E20.1.6.0", {"start": v(-18.35, 48.76) * mm, "mid": v(-18.7, 48.63) * mm, "end": v(-19.03, 48.5) * mm});
            skLineSegment(sketch, "E20.4.6.0", {"start": v(-18.15, 46.15) * mm, "end": v(-19.03, 48.5) * mm});
            skArc(sketch, "E20.7.6.0", {"start": v(-18.15, 46.15) * mm, "mid": v(-18.97, 45.82) * mm, "end": v(-19.79, 45.47) * mm});
            skLineSegment(sketch, "E20.11.6.0", {"start": v(-19.79, 45.47) * mm, "end": v(-20.82, 47.76) * mm});
            skArc(sketch, "E20.14.6.0", {"start": v(-20.82, 47.76) * mm, "mid": v(-21.16, 47.6) * mm, "end": v(-21.5, 47.45) * mm});
            skArc(sketch, "E20.1.7.0", {"start": v(-21.5, 47.45) * mm, "mid": v(-21.83, 47.3) * mm, "end": v(-22.16, 47.15) * mm});
            skLineSegment(sketch, "E20.4.7.0", {"start": v(-21.13, 44.86) * mm, "end": v(-22.16, 47.15) * mm});
            skArc(sketch, "E20.7.7.0", {"start": v(-21.13, 44.86) * mm, "mid": v(-21.93, 44.48) * mm, "end": v(-22.72, 44.08) * mm});
            skLineSegment(sketch, "E20.11.7.0", {"start": v(-22.72, 44.08) * mm, "end": v(-23.9, 46.3) * mm});
            skArc(sketch, "E20.14.7.0", {"start": v(-23.9, 46.3) * mm, "mid": v(-24.23, 46.12) * mm, "end": v(-24.56, 45.95) * mm});
            skArc(sketch, "E20.1.8.0", {"start": v(-24.56, 45.95) * mm, "mid": v(-24.88, 45.77) * mm, "end": v(-25.2, 45.6) * mm});
            skLineSegment(sketch, "E20.4.8.0", {"start": v(-24.01, 43.39) * mm, "end": v(-25.2, 45.6) * mm});
            skArc(sketch, "E20.7.8.0", {"start": v(-24.01, 43.39) * mm, "mid": v(-24.79, 42.95) * mm, "end": v(-25.55, 42.5) * mm});
            skLineSegment(sketch, "E20.11.8.0", {"start": v(-25.55, 42.5) * mm, "end": v(-26.88, 44.63) * mm});
            skArc(sketch, "E20.14.8.0", {"start": v(-26.88, 44.63) * mm, "mid": v(-27.2, 44.44) * mm, "end": v(-27.51, 44.24) * mm});
            skArc(sketch, "E20.1.9.0", {"start": v(-27.51, 44.24) * mm, "mid": v(-27.82, 44.05) * mm, "end": v(-28.13, 43.85) * mm});
            skLineSegment(sketch, "E20.4.9.0", {"start": v(-26.8, 41.72) * mm, "end": v(-28.13, 43.85) * mm});
            skArc(sketch, "E20.7.9.0", {"start": v(-26.8, 41.72) * mm, "mid": v(-27.54, 41.24) * mm, "end": v(-28.28, 40.74) * mm});
            skLineSegment(sketch, "E20.11.9.0", {"start": v(-28.28, 40.74) * mm, "end": v(-29.74, 42.78) * mm});
            skArc(sketch, "E20.14.9.0", {"start": v(-29.74, 42.78) * mm, "mid": v(-30.04, 42.56) * mm, "end": v(-30.35, 42.35) * mm});
            skArc(sketch, "E20.1.10.0", {"start": v(-30.35, 42.35) * mm, "mid": v(-30.64, 42.13) * mm, "end": v(-30.93, 41.92) * mm});
            skLineSegment(sketch, "E20.4.10.0", {"start": v(-29.47, 39.88) * mm, "end": v(-30.93, 41.92) * mm});
            skArc(sketch, "E20.7.10.0", {"start": v(-29.47, 39.88) * mm, "mid": v(-30.18, 39.35) * mm, "end": v(-30.88, 38.8) * mm});
            skLineSegment(sketch, "E20.11.10.0", {"start": v(-30.88, 38.8) * mm, "end": v(-32.47, 40.74) * mm});
            skArc(sketch, "E20.14.10.0", {"start": v(-32.47, 40.74) * mm, "mid": v(-32.76, 40.5) * mm, "end": v(-33.05, 40.27) * mm});
            skArc(sketch, "E20.1.11.0", {"start": v(-33.05, 40.27) * mm, "mid": v(-33.33, 40.04) * mm, "end": v(-33.6, 39.8) * mm});
            skLineSegment(sketch, "E20.4.11.0", {"start": v(-32.02, 37.87) * mm, "end": v(-33.6, 39.8) * mm});
            skArc(sketch, "E20.7.11.0", {"start": v(-32.02, 37.87) * mm, "mid": v(-32.69, 37.29) * mm, "end": v(-33.35, 36.7) * mm});
            skLineSegment(sketch, "E20.11.11.0", {"start": v(-33.35, 36.7) * mm, "end": v(-35.07, 38.53) * mm});
            skArc(sketch, "E20.14.11.0", {"start": v(-35.07, 38.53) * mm, "mid": v(-35.34, 38.28) * mm, "end": v(-35.61, 38.02) * mm});
            skArc(sketch, "E20.1.12.0", {"start": v(-35.61, 38.02) * mm, "mid": v(-35.88, 37.77) * mm, "end": v(-36.14, 37.52) * mm});
            skLineSegment(sketch, "E20.4.12.0", {"start": v(-34.43, 35.7) * mm, "end": v(-36.14, 37.52) * mm});
            skArc(sketch, "E20.7.12.0", {"start": v(-34.43, 35.7) * mm, "mid": v(-35.06, 35.07) * mm, "end": v(-35.68, 34.44) * mm});
            skLineSegment(sketch, "E20.11.12.0", {"start": v(-35.68, 34.44) * mm, "end": v(-37.51, 36.15) * mm});
            skArc(sketch, "E20.14.12.0", {"start": v(-37.51, 36.15) * mm, "mid": v(-37.77, 35.88) * mm, "end": v(-38.02, 35.61) * mm});
            skArc(sketch, "E20.1.13.0", {"start": v(-38.02, 35.61) * mm, "mid": v(-38.27, 35.35) * mm, "end": v(-38.52, 35.08) * mm});
            skLineSegment(sketch, "E20.4.13.0", {"start": v(-36.69, 33.36) * mm, "end": v(-38.52, 35.08) * mm});
            skArc(sketch, "E20.7.13.0", {"start": v(-36.69, 33.36) * mm, "mid": v(-37.28, 32.7) * mm, "end": v(-37.86, 32.03) * mm});
            skLineSegment(sketch, "E20.11.13.0", {"start": v(-37.86, 32.03) * mm, "end": v(-39.8, 33.62) * mm});
            skArc(sketch, "E20.14.13.0", {"start": v(-39.8, 33.62) * mm, "mid": v(-40.03, 33.34) * mm, "end": v(-40.27, 33.05) * mm});
            skArc(sketch, "E20.1.14.0", {"start": v(-40.27, 33.05) * mm, "mid": v(-40.5, 32.77) * mm, "end": v(-40.73, 32.49) * mm});
            skLineSegment(sketch, "E20.4.14.0", {"start": v(-38.79, 30.9) * mm, "end": v(-40.73, 32.49) * mm});
            skArc(sketch, "E20.7.14.0", {"start": v(-38.79, 30.9) * mm, "mid": v(-39.34, 30.2) * mm, "end": v(-39.87, 29.48) * mm});
            skLineSegment(sketch, "E20.11.14.0", {"start": v(-39.87, 29.48) * mm, "end": v(-41.9, 30.95) * mm});
            skArc(sketch, "E20.14.14.0", {"start": v(-41.9, 30.95) * mm, "mid": v(-42.13, 30.65) * mm, "end": v(-42.35, 30.35) * mm});
            skArc(sketch, "E20.1.15.0", {"start": v(-42.35, 30.35) * mm, "mid": v(-42.56, 30.05) * mm, "end": v(-42.77, 29.75) * mm});
            skLineSegment(sketch, "E20.4.15.0", {"start": v(-40.73, 28.3) * mm, "end": v(-42.77, 29.75) * mm});
            skArc(sketch, "E20.7.15.0", {"start": v(-40.73, 28.3) * mm, "mid": v(-41.23, 27.56) * mm, "end": v(-41.71, 26.81) * mm});
            skLineSegment(sketch, "E20.11.15.0", {"start": v(-41.71, 26.81) * mm, "end": v(-43.84, 28.14) * mm});
            skArc(sketch, "E20.14.15.0", {"start": v(-43.84, 28.14) * mm, "mid": v(-44.04, 27.83) * mm, "end": v(-44.24, 27.51) * mm});
            skArc(sketch, "E20.1.16.0", {"start": v(-44.24, 27.51) * mm, "mid": v(-44.43, 27.2) * mm, "end": v(-44.62, 26.9) * mm});
            skLineSegment(sketch, "E20.4.16.0", {"start": v(-42.49, 25.57) * mm, "end": v(-44.62, 26.9) * mm});
            skArc(sketch, "E20.7.16.0", {"start": v(-42.49, 25.57) * mm, "mid": v(-42.94, 24.8) * mm, "end": v(-43.38, 24.03) * mm});
            skLineSegment(sketch, "E20.11.16.0", {"start": v(-43.38, 24.03) * mm, "end": v(-45.6, 25.21) * mm});
            skArc(sketch, "E20.14.16.0", {"start": v(-45.6, 25.21) * mm, "mid": v(-45.77, 24.89) * mm, "end": v(-45.95, 24.56) * mm});
            skArc(sketch, "E20.1.17.0", {"start": v(-45.95, 24.56) * mm, "mid": v(-46.12, 24.24) * mm, "end": v(-46.28, 23.92) * mm});
            skLineSegment(sketch, "E20.4.17.0", {"start": v(-44.07, 22.73) * mm, "end": v(-46.28, 23.92) * mm});
            skArc(sketch, "E20.7.17.0", {"start": v(-44.07, 22.73) * mm, "mid": v(-44.47, 21.94) * mm, "end": v(-44.86, 21.14) * mm});
            skLineSegment(sketch, "E20.11.17.0", {"start": v(-44.86, 21.14) * mm, "end": v(-47.14, 22.18) * mm});
            skArc(sketch, "E20.14.17.0", {"start": v(-47.14, 22.18) * mm, "mid": v(-47.3, 21.84) * mm, "end": v(-47.45, 21.5) * mm});
            skArc(sketch, "E20.1.18.0", {"start": v(-47.45, 21.5) * mm, "mid": v(-47.6, 21.17) * mm, "end": v(-47.75, 20.84) * mm});
            skLineSegment(sketch, "E20.4.18.0", {"start": v(-45.46, 19.8) * mm, "end": v(-47.75, 20.84) * mm});
            skArc(sketch, "E20.7.18.0", {"start": v(-45.46, 19.8) * mm, "mid": v(-45.81, 18.98) * mm, "end": v(-46.14, 18.16) * mm});
            skLineSegment(sketch, "E20.11.18.0", {"start": v(-46.14, 18.16) * mm, "end": v(-48.5, 19.04) * mm});
            skArc(sketch, "E20.14.18.0", {"start": v(-48.5, 19.04) * mm, "mid": v(-48.63, 18.7) * mm, "end": v(-48.76, 18.35) * mm});
            skArc(sketch, "E20.1.19.0", {"start": v(-48.76, 18.35) * mm, "mid": v(-48.88, 18.01) * mm, "end": v(-49, 17.67) * mm});
            skLineSegment(sketch, "E20.4.19.0", {"start": v(-46.66, 16.79) * mm, "end": v(-49, 17.67) * mm});
            skArc(sketch, "E20.7.19.0", {"start": v(-46.66, 16.79) * mm, "mid": v(-46.95, 15.95) * mm, "end": v(-47.23, 15.1) * mm});
            skLineSegment(sketch, "E20.11.19.0", {"start": v(-47.23, 15.1) * mm, "end": v(-49.63, 15.83) * mm});
            skArc(sketch, "E20.14.19.0", {"start": v(-49.63, 15.83) * mm, "mid": v(-49.74, 15.48) * mm, "end": v(-49.85, 15.12) * mm});
            skArc(sketch, "E20.1.20.0", {"start": v(-49.85, 15.12) * mm, "mid": v(-49.96, 14.77) * mm, "end": v(-50.06, 14.43) * mm});
            skLineSegment(sketch, "E20.4.20.0", {"start": v(-47.66, 13.7) * mm, "end": v(-50.06, 14.43) * mm});
            skArc(sketch, "E20.7.20.0", {"start": v(-47.66, 13.7) * mm, "mid": v(-47.9, 12.84) * mm, "end": v(-48.12, 11.98) * mm});
            skLineSegment(sketch, "E20.11.20.0", {"start": v(-48.12, 11.98) * mm, "end": v(-50.56, 12.55) * mm});
            skArc(sketch, "E20.14.20.0", {"start": v(-50.56, 12.55) * mm, "mid": v(-50.65, 12.2) * mm, "end": v(-50.74, 11.83) * mm});
            skArc(sketch, "E20.1.21.0", {"start": v(-50.74, 11.83) * mm, "mid": v(-50.82, 11.48) * mm, "end": v(-50.9, 11.12) * mm});
            skLineSegment(sketch, "E20.4.21.0", {"start": v(-48.45, 10.55) * mm, "end": v(-50.9, 11.12) * mm});
            skArc(sketch, "E20.7.21.0", {"start": v(-48.45, 10.55) * mm, "mid": v(-48.63, 9.68) * mm, "end": v(-48.8, 8.8) * mm});
            skLineSegment(sketch, "E20.11.21.0", {"start": v(-48.8, 8.8) * mm, "end": v(-51.27, 9.22) * mm});
            skArc(sketch, "E20.14.21.0", {"start": v(-51.27, 9.22) * mm, "mid": v(-51.34, 8.85) * mm, "end": v(-51.4, 8.49) * mm});
            skArc(sketch, "E20.1.22.0", {"start": v(-51.4, 8.49) * mm, "mid": v(-51.46, 8.13) * mm, "end": v(-51.51, 7.77) * mm});
            skLineSegment(sketch, "E20.4.22.0", {"start": v(-49.04, 7.36) * mm, "end": v(-51.51, 7.77) * mm});
            skArc(sketch, "E20.7.22.0", {"start": v(-49.04, 7.36) * mm, "mid": v(-49.16, 6.48) * mm, "end": v(-49.27, 5.6) * mm});
            skLineSegment(sketch, "E20.11.22.0", {"start": v(-49.27, 5.6) * mm, "end": v(-51.77, 5.85) * mm});
            skArc(sketch, "E20.14.22.0", {"start": v(-51.77, 5.85) * mm, "mid": v(-51.8, 5.48) * mm, "end": v(-51.85, 5.1) * mm});
            skArc(sketch, "E20.1.23.0", {"start": v(-51.85, 5.1) * mm, "mid": v(-51.88, 4.74) * mm, "end": v(-51.91, 4.38) * mm});
            skLineSegment(sketch, "E20.4.23.0", {"start": v(-49.42, 4.14) * mm, "end": v(-51.91, 4.38) * mm});
            skArc(sketch, "E20.7.23.0", {"start": v(-49.42, 4.14) * mm, "mid": v(-49.48, 3.25) * mm, "end": v(-49.53, 2.36) * mm});
            skLineSegment(sketch, "E20.11.23.0", {"start": v(-49.53, 2.36) * mm, "end": v(-52.04, 2.45) * mm});
            skArc(sketch, "E20.14.23.0", {"start": v(-52.04, 2.45) * mm, "mid": v(-52.06, 2.08) * mm, "end": v(-52.07, 1.7) * mm});
            skArc(sketch, "E20.1.24.0", {"start": v(-52.07, 1.7) * mm, "mid": v(-52.08, 1.34) * mm, "end": v(-52.09, 0.98) * mm});
            skLineSegment(sketch, "E20.4.24.0", {"start": v(-49.58, 0.9) * mm, "end": v(-52.09, 0.98) * mm});
            skArc(sketch, "E20.7.24.0", {"start": v(-49.58, 0.9) * mm, "mid": v(-49.59, 0) * mm, "end": v(-49.58, -0.88) * mm});
            skLineSegment(sketch, "E20.11.24.0", {"start": v(-49.58, -0.88) * mm, "end": v(-52.09, -0.96) * mm});
            skArc(sketch, "E20.14.24.0", {"start": v(-52.09, -0.96) * mm, "mid": v(-52.08, -1.33) * mm, "end": v(-52.07, -1.7) * mm});
            skArc(sketch, "E20.1.25.0", {"start": v(-52.07, -1.7) * mm, "mid": v(-52.06, -2.07) * mm, "end": v(-52.04, -2.43) * mm});
            skLineSegment(sketch, "E20.4.25.0", {"start": v(-49.53, -2.35) * mm, "end": v(-52.04, -2.43) * mm});
            skArc(sketch, "E20.7.25.0", {"start": v(-49.53, -2.35) * mm, "mid": v(-49.48, -3.24) * mm, "end": v(-49.42, -4.12) * mm});
            skLineSegment(sketch, "E20.11.25.0", {"start": v(-49.42, -4.12) * mm, "end": v(-51.91, -4.37) * mm});
            skArc(sketch, "E20.14.25.0", {"start": v(-51.91, -4.37) * mm, "mid": v(-51.88, -4.74) * mm, "end": v(-51.85, -5.1) * mm});
            skArc(sketch, "E20.1.26.0", {"start": v(-51.85, -5.1) * mm, "mid": v(-51.8, -5.47) * mm, "end": v(-51.77, -5.83) * mm});
            skLineSegment(sketch, "E20.4.26.0", {"start": v(-49.27, -5.58) * mm, "end": v(-51.77, -5.83) * mm});
            skArc(sketch, "E20.7.26.0", {"start": v(-49.27, -5.58) * mm, "mid": v(-49.17, -6.46) * mm, "end": v(-49.04, -7.34) * mm});
            skLineSegment(sketch, "E20.11.26.0", {"start": v(-49.04, -7.34) * mm, "end": v(-51.52, -7.75) * mm});
            skArc(sketch, "E20.14.26.0", {"start": v(-51.52, -7.75) * mm, "mid": v(-51.46, -8.12) * mm, "end": v(-51.4, -8.49) * mm});
            skArc(sketch, "E20.1.27.0", {"start": v(-51.4, -8.49) * mm, "mid": v(-51.34, -8.84) * mm, "end": v(-51.28, -9.2) * mm});
            skLineSegment(sketch, "E20.4.27.0", {"start": v(-48.8, -8.8) * mm, "end": v(-51.28, -9.2) * mm});
            skArc(sketch, "E20.7.27.0", {"start": v(-48.8, -8.8) * mm, "mid": v(-48.64, -9.67) * mm, "end": v(-48.46, -10.54) * mm});
            skLineSegment(sketch, "E20.11.27.0", {"start": v(-48.46, -10.54) * mm, "end": v(-50.9, -11.1) * mm});
            skArc(sketch, "E20.14.27.0", {"start": v(-50.9, -11.1) * mm, "mid": v(-50.82, -11.47) * mm, "end": v(-50.74, -11.83) * mm});
            skArc(sketch, "E20.1.28.0", {"start": v(-50.74, -11.83) * mm, "mid": v(-50.65, -12.18) * mm, "end": v(-50.57, -12.54) * mm});
            skLineSegment(sketch, "E20.4.28.0", {"start": v(-48.12, -11.97) * mm, "end": v(-50.57, -12.54) * mm});
            skArc(sketch, "E20.7.28.0", {"start": v(-48.12, -11.97) * mm, "mid": v(-47.9, -12.83) * mm, "end": v(-47.66, -13.68) * mm});
            skLineSegment(sketch, "E20.11.28.0", {"start": v(-47.66, -13.68) * mm, "end": v(-50.06, -14.41) * mm});
            skArc(sketch, "E20.14.28.0", {"start": v(-50.06, -14.41) * mm, "mid": v(-49.96, -14.77) * mm, "end": v(-49.85, -15.12) * mm});
            skArc(sketch, "E20.1.29.0", {"start": v(-49.85, -15.12) * mm, "mid": v(-49.75, -15.47) * mm, "end": v(-49.64, -15.82) * mm});
            skLineSegment(sketch, "E20.4.29.0", {"start": v(-47.24, -15.09) * mm, "end": v(-49.64, -15.82) * mm});
            skArc(sketch, "E20.7.29.0", {"start": v(-47.24, -15.09) * mm, "mid": v(-46.96, -15.93) * mm, "end": v(-46.67, -16.77) * mm});
            skLineSegment(sketch, "E20.11.29.0", {"start": v(-46.67, -16.77) * mm, "end": v(-49.01, -17.65) * mm});
            skArc(sketch, "E20.14.29.0", {"start": v(-49.01, -17.65) * mm, "mid": v(-48.89, -18) * mm, "end": v(-48.76, -18.35) * mm});
            skArc(sketch, "E20.1.30.0", {"start": v(-48.76, -18.35) * mm, "mid": v(-48.63, -18.7) * mm, "end": v(-48.5, -19.03) * mm});
            skLineSegment(sketch, "E20.4.30.0", {"start": v(-46.15, -18.15) * mm, "end": v(-48.5, -19.03) * mm});
            skArc(sketch, "E20.7.30.0", {"start": v(-46.15, -18.15) * mm, "mid": v(-45.82, -18.97) * mm, "end": v(-45.47, -19.79) * mm});
            skLineSegment(sketch, "E20.11.30.0", {"start": v(-45.47, -19.79) * mm, "end": v(-47.76, -20.82) * mm});
            skArc(sketch, "E20.14.30.0", {"start": v(-47.76, -20.82) * mm, "mid": v(-47.6, -21.16) * mm, "end": v(-47.45, -21.5) * mm});
            skArc(sketch, "E20.1.31.0", {"start": v(-47.45, -21.5) * mm, "mid": v(-47.3, -21.83) * mm, "end": v(-47.15, -22.16) * mm});
            skLineSegment(sketch, "E20.4.31.0", {"start": v(-44.86, -21.13) * mm, "end": v(-47.15, -22.16) * mm});
            skArc(sketch, "E20.7.31.0", {"start": v(-44.86, -21.13) * mm, "mid": v(-44.48, -21.93) * mm, "end": v(-44.08, -22.72) * mm});
            skLineSegment(sketch, "E20.11.31.0", {"start": v(-44.08, -22.72) * mm, "end": v(-46.3, -23.9) * mm});
            skArc(sketch, "E20.14.31.0", {"start": v(-46.3, -23.9) * mm, "mid": v(-46.12, -24.23) * mm, "end": v(-45.95, -24.56) * mm});
            skArc(sketch, "E20.1.32.0", {"start": v(-45.95, -24.56) * mm, "mid": v(-45.77, -24.88) * mm, "end": v(-45.6, -25.2) * mm});
            skLineSegment(sketch, "E20.4.32.0", {"start": v(-43.39, -24.01) * mm, "end": v(-45.6, -25.2) * mm});
            skArc(sketch, "E20.7.32.0", {"start": v(-43.39, -24.01) * mm, "mid": v(-42.95, -24.79) * mm, "end": v(-42.5, -25.55) * mm});
            skLineSegment(sketch, "E20.11.32.0", {"start": v(-42.5, -25.55) * mm, "end": v(-44.63, -26.88) * mm});
            skArc(sketch, "E20.14.32.0", {"start": v(-44.63, -26.88) * mm, "mid": v(-44.44, -27.2) * mm, "end": v(-44.24, -27.51) * mm});
            skArc(sketch, "E20.1.33.0", {"start": v(-44.24, -27.51) * mm, "mid": v(-44.05, -27.82) * mm, "end": v(-43.85, -28.13) * mm});
            skLineSegment(sketch, "E20.4.33.0", {"start": v(-41.72, -26.8) * mm, "end": v(-43.85, -28.13) * mm});
            skArc(sketch, "E20.7.33.0", {"start": v(-41.72, -26.8) * mm, "mid": v(-41.24, -27.54) * mm, "end": v(-40.74, -28.28) * mm});
            skLineSegment(sketch, "E20.11.33.0", {"start": v(-40.74, -28.28) * mm, "end": v(-42.78, -29.74) * mm});
            skArc(sketch, "E20.14.33.0", {"start": v(-42.78, -29.74) * mm, "mid": v(-42.56, -30.04) * mm, "end": v(-42.35, -30.35) * mm});
            skArc(sketch, "E20.1.34.0", {"start": v(-42.35, -30.35) * mm, "mid": v(-42.13, -30.64) * mm, "end": v(-41.92, -30.93) * mm});
            skLineSegment(sketch, "E20.4.34.0", {"start": v(-39.88, -29.47) * mm, "end": v(-41.92, -30.93) * mm});
            skArc(sketch, "E20.7.34.0", {"start": v(-39.88, -29.47) * mm, "mid": v(-39.35, -30.18) * mm, "end": v(-38.8, -30.88) * mm});
            skLineSegment(sketch, "E20.11.34.0", {"start": v(-38.8, -30.88) * mm, "end": v(-40.74, -32.47) * mm});
            skArc(sketch, "E20.14.34.0", {"start": v(-40.74, -32.47) * mm, "mid": v(-40.5, -32.76) * mm, "end": v(-40.27, -33.05) * mm});
            skArc(sketch, "E20.1.35.0", {"start": v(-40.27, -33.05) * mm, "mid": v(-40.04, -33.33) * mm, "end": v(-39.8, -33.6) * mm});
            skLineSegment(sketch, "E20.4.35.0", {"start": v(-37.87, -32.02) * mm, "end": v(-39.8, -33.6) * mm});
            skArc(sketch, "E20.7.35.0", {"start": v(-37.87, -32.02) * mm, "mid": v(-37.29, -32.69) * mm, "end": v(-36.7, -33.35) * mm});
            skLineSegment(sketch, "E20.11.35.0", {"start": v(-36.7, -33.35) * mm, "end": v(-38.53, -35.07) * mm});
            skArc(sketch, "E20.14.35.0", {"start": v(-38.53, -35.07) * mm, "mid": v(-38.28, -35.34) * mm, "end": v(-38.02, -35.61) * mm});
            skArc(sketch, "E20.1.36.0", {"start": v(-38.02, -35.61) * mm, "mid": v(-37.77, -35.88) * mm, "end": v(-37.52, -36.14) * mm});
            skLineSegment(sketch, "E20.4.36.0", {"start": v(-35.7, -34.43) * mm, "end": v(-37.52, -36.14) * mm});
            skArc(sketch, "E20.7.36.0", {"start": v(-35.7, -34.43) * mm, "mid": v(-35.07, -35.06) * mm, "end": v(-34.44, -35.68) * mm});
            skLineSegment(sketch, "E20.11.36.0", {"start": v(-34.44, -35.68) * mm, "end": v(-36.15, -37.51) * mm});
            skArc(sketch, "E20.14.36.0", {"start": v(-36.15, -37.51) * mm, "mid": v(-35.88, -37.77) * mm, "end": v(-35.61, -38.02) * mm});
            skArc(sketch, "E20.1.37.0", {"start": v(-35.61, -38.02) * mm, "mid": v(-35.35, -38.27) * mm, "end": v(-35.08, -38.52) * mm});
            skLineSegment(sketch, "E20.4.37.0", {"start": v(-33.36, -36.69) * mm, "end": v(-35.08, -38.52) * mm});
            skArc(sketch, "E20.7.37.0", {"start": v(-33.36, -36.69) * mm, "mid": v(-32.7, -37.28) * mm, "end": v(-32.03, -37.86) * mm});
            skLineSegment(sketch, "E20.11.37.0", {"start": v(-32.03, -37.86) * mm, "end": v(-33.62, -39.8) * mm});
            skArc(sketch, "E20.14.37.0", {"start": v(-33.62, -39.8) * mm, "mid": v(-33.34, -40.03) * mm, "end": v(-33.05, -40.27) * mm});
            skArc(sketch, "E20.1.38.0", {"start": v(-33.05, -40.27) * mm, "mid": v(-32.77, -40.5) * mm, "end": v(-32.49, -40.73) * mm});
            skLineSegment(sketch, "E20.4.38.0", {"start": v(-30.9, -38.79) * mm, "end": v(-32.49, -40.73) * mm});
            skArc(sketch, "E20.7.38.0", {"start": v(-30.9, -38.79) * mm, "mid": v(-30.2, -39.34) * mm, "end": v(-29.48, -39.87) * mm});
            skLineSegment(sketch, "E20.11.38.0", {"start": v(-29.48, -39.87) * mm, "end": v(-30.95, -41.9) * mm});
            skArc(sketch, "E20.14.38.0", {"start": v(-30.95, -41.9) * mm, "mid": v(-30.65, -42.13) * mm, "end": v(-30.35, -42.35) * mm});
            skArc(sketch, "E20.1.39.0", {"start": v(-30.35, -42.35) * mm, "mid": v(-30.05, -42.56) * mm, "end": v(-29.75, -42.77) * mm});
            skLineSegment(sketch, "E20.4.39.0", {"start": v(-28.3, -40.73) * mm, "end": v(-29.75, -42.77) * mm});
            skArc(sketch, "E20.7.39.0", {"start": v(-28.3, -40.73) * mm, "mid": v(-27.56, -41.23) * mm, "end": v(-26.81, -41.71) * mm});
            skLineSegment(sketch, "E20.11.39.0", {"start": v(-26.81, -41.71) * mm, "end": v(-28.14, -43.84) * mm});
            skArc(sketch, "E20.14.39.0", {"start": v(-28.14, -43.84) * mm, "mid": v(-27.83, -44.04) * mm, "end": v(-27.51, -44.24) * mm});
            skArc(sketch, "E20.1.40.0", {"start": v(-27.51, -44.24) * mm, "mid": v(-27.2, -44.43) * mm, "end": v(-26.9, -44.62) * mm});
            skLineSegment(sketch, "E20.4.40.0", {"start": v(-25.57, -42.49) * mm, "end": v(-26.9, -44.62) * mm});
            skArc(sketch, "E20.7.40.0", {"start": v(-25.57, -42.49) * mm, "mid": v(-24.8, -42.94) * mm, "end": v(-24.03, -43.38) * mm});
            skLineSegment(sketch, "E20.11.40.0", {"start": v(-24.03, -43.38) * mm, "end": v(-25.21, -45.6) * mm});
            skArc(sketch, "E20.14.40.0", {"start": v(-25.21, -45.6) * mm, "mid": v(-24.89, -45.77) * mm, "end": v(-24.56, -45.95) * mm});
            skArc(sketch, "E20.1.41.0", {"start": v(-24.56, -45.95) * mm, "mid": v(-24.24, -46.12) * mm, "end": v(-23.92, -46.28) * mm});
            skLineSegment(sketch, "E20.4.41.0", {"start": v(-22.73, -44.07) * mm, "end": v(-23.92, -46.28) * mm});
            skArc(sketch, "E20.7.41.0", {"start": v(-22.73, -44.07) * mm, "mid": v(-21.94, -44.47) * mm, "end": v(-21.14, -44.86) * mm});
            skLineSegment(sketch, "E20.11.41.0", {"start": v(-21.14, -44.86) * mm, "end": v(-22.18, -47.14) * mm});
            skArc(sketch, "E20.14.41.0", {"start": v(-22.18, -47.14) * mm, "mid": v(-21.84, -47.3) * mm, "end": v(-21.5, -47.45) * mm});
            skArc(sketch, "E20.1.42.0", {"start": v(-21.5, -47.45) * mm, "mid": v(-21.17, -47.6) * mm, "end": v(-20.84, -47.75) * mm});
            skLineSegment(sketch, "E20.4.42.0", {"start": v(-19.8, -45.46) * mm, "end": v(-20.84, -47.75) * mm});
            skArc(sketch, "E20.7.42.0", {"start": v(-19.8, -45.46) * mm, "mid": v(-18.98, -45.81) * mm, "end": v(-18.16, -46.14) * mm});
            skLineSegment(sketch, "E20.11.42.0", {"start": v(-18.16, -46.14) * mm, "end": v(-19.04, -48.5) * mm});
            skArc(sketch, "E20.14.42.0", {"start": v(-19.04, -48.5) * mm, "mid": v(-18.7, -48.63) * mm, "end": v(-18.35, -48.76) * mm});
            skArc(sketch, "E20.1.43.0", {"start": v(-18.35, -48.76) * mm, "mid": v(-18.01, -48.88) * mm, "end": v(-17.67, -49) * mm});
            skLineSegment(sketch, "E20.4.43.0", {"start": v(-16.79, -46.66) * mm, "end": v(-17.67, -49) * mm});
            skArc(sketch, "E20.7.43.0", {"start": v(-16.79, -46.66) * mm, "mid": v(-15.95, -46.95) * mm, "end": v(-15.1, -47.23) * mm});
            skLineSegment(sketch, "E20.11.43.0", {"start": v(-15.1, -47.23) * mm, "end": v(-15.83, -49.63) * mm});
            skArc(sketch, "E20.14.43.0", {"start": v(-15.83, -49.63) * mm, "mid": v(-15.48, -49.74) * mm, "end": v(-15.12, -49.85) * mm});
            skArc(sketch, "E20.1.44.0", {"start": v(-15.12, -49.85) * mm, "mid": v(-14.77, -49.96) * mm, "end": v(-14.43, -50.06) * mm});
            skLineSegment(sketch, "E20.4.44.0", {"start": v(-13.7, -47.66) * mm, "end": v(-14.43, -50.06) * mm});
            skArc(sketch, "E20.7.44.0", {"start": v(-13.7, -47.66) * mm, "mid": v(-12.84, -47.9) * mm, "end": v(-11.98, -48.12) * mm});
            skLineSegment(sketch, "E20.11.44.0", {"start": v(-11.98, -48.12) * mm, "end": v(-12.55, -50.56) * mm});
            skArc(sketch, "E20.14.44.0", {"start": v(-12.55, -50.56) * mm, "mid": v(-12.2, -50.65) * mm, "end": v(-11.83, -50.74) * mm});
            skArc(sketch, "E20.1.45.0", {"start": v(-11.83, -50.74) * mm, "mid": v(-11.48, -50.82) * mm, "end": v(-11.12, -50.9) * mm});
            skLineSegment(sketch, "E20.4.45.0", {"start": v(-10.55, -48.45) * mm, "end": v(-11.12, -50.9) * mm});
            skArc(sketch, "E20.7.45.0", {"start": v(-10.55, -48.45) * mm, "mid": v(-9.68, -48.63) * mm, "end": v(-8.8, -48.8) * mm});
            skLineSegment(sketch, "E20.11.45.0", {"start": v(-8.8, -48.8) * mm, "end": v(-9.22, -51.27) * mm});
            skArc(sketch, "E20.14.45.0", {"start": v(-9.22, -51.27) * mm, "mid": v(-8.85, -51.34) * mm, "end": v(-8.49, -51.4) * mm});
            skArc(sketch, "E20.1.46.0", {"start": v(-8.49, -51.4) * mm, "mid": v(-8.13, -51.46) * mm, "end": v(-7.77, -51.51) * mm});
            skLineSegment(sketch, "E20.4.46.0", {"start": v(-7.36, -49.04) * mm, "end": v(-7.77, -51.51) * mm});
            skArc(sketch, "E20.7.46.0", {"start": v(-7.36, -49.04) * mm, "mid": v(-6.48, -49.16) * mm, "end": v(-5.6, -49.27) * mm});
            skLineSegment(sketch, "E20.11.46.0", {"start": v(-5.6, -49.27) * mm, "end": v(-5.85, -51.77) * mm});
            skArc(sketch, "E20.14.46.0", {"start": v(-5.85, -51.77) * mm, "mid": v(-5.48, -51.8) * mm, "end": v(-5.1, -51.85) * mm});
            skArc(sketch, "E20.1.47.0", {"start": v(-5.1, -51.85) * mm, "mid": v(-4.74, -51.88) * mm, "end": v(-4.38, -51.91) * mm});
            skLineSegment(sketch, "E20.4.47.0", {"start": v(-4.14, -49.42) * mm, "end": v(-4.38, -51.91) * mm});
            skArc(sketch, "E20.7.47.0", {"start": v(-4.14, -49.42) * mm, "mid": v(-3.25, -49.48) * mm, "end": v(-2.36, -49.53) * mm});
            skLineSegment(sketch, "E20.11.47.0", {"start": v(-2.36, -49.53) * mm, "end": v(-2.45, -52.04) * mm});
            skArc(sketch, "E20.14.47.0", {"start": v(-2.45, -52.04) * mm, "mid": v(-2.08, -52.06) * mm, "end": v(-1.7, -52.07) * mm});
            skArc(sketch, "E20.1.48.0", {"start": v(-1.7, -52.07) * mm, "mid": v(-1.34, -52.08) * mm, "end": v(-0.98, -52.09) * mm});
            skLineSegment(sketch, "E20.4.48.0", {"start": v(-0.9, -49.58) * mm, "end": v(-0.98, -52.09) * mm});
            skArc(sketch, "E20.7.48.0", {"start": v(-0.9, -49.58) * mm, "mid": v(0, -49.59) * mm, "end": v(0.88, -49.58) * mm});
            skLineSegment(sketch, "E20.11.48.0", {"start": v(0.88, -49.58) * mm, "end": v(0.96, -52.09) * mm});
            skArc(sketch, "E20.14.48.0", {"start": v(0.96, -52.09) * mm, "mid": v(1.33, -52.08) * mm, "end": v(1.7, -52.07) * mm});
            skArc(sketch, "E20.1.49.0", {"start": v(1.7, -52.07) * mm, "mid": v(2.07, -52.06) * mm, "end": v(2.43, -52.04) * mm});
            skLineSegment(sketch, "E20.4.49.0", {"start": v(2.35, -49.53) * mm, "end": v(2.43, -52.04) * mm});
            skArc(sketch, "E20.7.49.0", {"start": v(2.35, -49.53) * mm, "mid": v(3.24, -49.48) * mm, "end": v(4.12, -49.42) * mm});
            skLineSegment(sketch, "E20.11.49.0", {"start": v(4.12, -49.42) * mm, "end": v(4.37, -51.91) * mm});
            skArc(sketch, "E20.14.49.0", {"start": v(4.37, -51.91) * mm, "mid": v(4.74, -51.88) * mm, "end": v(5.1, -51.85) * mm});
            skArc(sketch, "E20.1.50.0", {"start": v(5.1, -51.85) * mm, "mid": v(5.47, -51.8) * mm, "end": v(5.83, -51.77) * mm});
            skLineSegment(sketch, "E20.4.50.0", {"start": v(5.58, -49.27) * mm, "end": v(5.83, -51.77) * mm});
            skArc(sketch, "E20.7.50.0", {"start": v(5.58, -49.27) * mm, "mid": v(6.46, -49.17) * mm, "end": v(7.34, -49.04) * mm});
            skLineSegment(sketch, "E20.11.50.0", {"start": v(7.34, -49.04) * mm, "end": v(7.75, -51.52) * mm});
            skArc(sketch, "E20.14.50.0", {"start": v(7.75, -51.52) * mm, "mid": v(8.12, -51.46) * mm, "end": v(8.49, -51.4) * mm});
            skArc(sketch, "E20.1.51.0", {"start": v(8.49, -51.4) * mm, "mid": v(8.84, -51.34) * mm, "end": v(9.2, -51.28) * mm});
            skLineSegment(sketch, "E20.4.51.0", {"start": v(8.8, -48.8) * mm, "end": v(9.2, -51.28) * mm});
            skArc(sketch, "E20.7.51.0", {"start": v(8.8, -48.8) * mm, "mid": v(9.67, -48.64) * mm, "end": v(10.54, -48.46) * mm});
            skLineSegment(sketch, "E20.11.51.0", {"start": v(10.54, -48.46) * mm, "end": v(11.1, -50.9) * mm});
            skArc(sketch, "E20.14.51.0", {"start": v(11.1, -50.9) * mm, "mid": v(11.47, -50.82) * mm, "end": v(11.83, -50.74) * mm});
            skArc(sketch, "E20.1.52.0", {"start": v(11.83, -50.74) * mm, "mid": v(12.18, -50.65) * mm, "end": v(12.54, -50.57) * mm});
            skLineSegment(sketch, "E20.4.52.0", {"start": v(11.97, -48.12) * mm, "end": v(12.54, -50.57) * mm});
            skArc(sketch, "E20.7.52.0", {"start": v(11.97, -48.12) * mm, "mid": v(12.83, -47.9) * mm, "end": v(13.68, -47.66) * mm});
            skLineSegment(sketch, "E20.11.52.0", {"start": v(13.68, -47.66) * mm, "end": v(14.41, -50.06) * mm});
            skArc(sketch, "E20.14.52.0", {"start": v(14.41, -50.06) * mm, "mid": v(14.77, -49.96) * mm, "end": v(15.12, -49.85) * mm});
            skArc(sketch, "E20.1.53.0", {"start": v(15.12, -49.85) * mm, "mid": v(15.47, -49.75) * mm, "end": v(15.82, -49.64) * mm});
            skLineSegment(sketch, "E20.4.53.0", {"start": v(15.09, -47.24) * mm, "end": v(15.82, -49.64) * mm});
            skArc(sketch, "E20.7.53.0", {"start": v(15.09, -47.24) * mm, "mid": v(15.93, -46.96) * mm, "end": v(16.77, -46.67) * mm});
            skLineSegment(sketch, "E20.11.53.0", {"start": v(16.77, -46.67) * mm, "end": v(17.65, -49.01) * mm});
            skArc(sketch, "E20.14.53.0", {"start": v(17.65, -49.01) * mm, "mid": v(18, -48.89) * mm, "end": v(18.35, -48.76) * mm});
            skArc(sketch, "E20.1.54.0", {"start": v(18.35, -48.76) * mm, "mid": v(18.7, -48.63) * mm, "end": v(19.03, -48.5) * mm});
            skLineSegment(sketch, "E20.4.54.0", {"start": v(18.15, -46.15) * mm, "end": v(19.03, -48.5) * mm});
            skArc(sketch, "E20.7.54.0", {"start": v(18.15, -46.15) * mm, "mid": v(18.97, -45.82) * mm, "end": v(19.79, -45.47) * mm});
            skLineSegment(sketch, "E20.11.54.0", {"start": v(19.79, -45.47) * mm, "end": v(20.82, -47.76) * mm});
            skArc(sketch, "E20.14.54.0", {"start": v(20.82, -47.76) * mm, "mid": v(21.16, -47.6) * mm, "end": v(21.5, -47.45) * mm});
            skArc(sketch, "E20.1.55.0", {"start": v(21.5, -47.45) * mm, "mid": v(21.83, -47.3) * mm, "end": v(22.16, -47.15) * mm});
            skLineSegment(sketch, "E20.4.55.0", {"start": v(21.13, -44.86) * mm, "end": v(22.16, -47.15) * mm});
            skArc(sketch, "E20.7.55.0", {"start": v(21.13, -44.86) * mm, "mid": v(21.93, -44.48) * mm, "end": v(22.72, -44.08) * mm});
            skLineSegment(sketch, "E20.11.55.0", {"start": v(22.72, -44.08) * mm, "end": v(23.9, -46.3) * mm});
            skArc(sketch, "E20.14.55.0", {"start": v(23.9, -46.3) * mm, "mid": v(24.23, -46.12) * mm, "end": v(24.56, -45.95) * mm});
            skArc(sketch, "E20.1.56.0", {"start": v(24.56, -45.95) * mm, "mid": v(24.88, -45.77) * mm, "end": v(25.2, -45.6) * mm});
            skLineSegment(sketch, "E20.4.56.0", {"start": v(24.01, -43.39) * mm, "end": v(25.2, -45.6) * mm});
            skArc(sketch, "E20.7.56.0", {"start": v(24.01, -43.39) * mm, "mid": v(24.79, -42.95) * mm, "end": v(25.55, -42.5) * mm});
            skLineSegment(sketch, "E20.11.56.0", {"start": v(25.55, -42.5) * mm, "end": v(26.88, -44.63) * mm});
            skArc(sketch, "E20.14.56.0", {"start": v(26.88, -44.63) * mm, "mid": v(27.2, -44.44) * mm, "end": v(27.51, -44.24) * mm});
            skArc(sketch, "E20.1.57.0", {"start": v(27.51, -44.24) * mm, "mid": v(27.82, -44.05) * mm, "end": v(28.13, -43.85) * mm});
            skLineSegment(sketch, "E20.4.57.0", {"start": v(26.8, -41.72) * mm, "end": v(28.13, -43.85) * mm});
            skArc(sketch, "E20.7.57.0", {"start": v(26.8, -41.72) * mm, "mid": v(27.54, -41.24) * mm, "end": v(28.28, -40.74) * mm});
            skLineSegment(sketch, "E20.11.57.0", {"start": v(28.28, -40.74) * mm, "end": v(29.74, -42.78) * mm});
            skArc(sketch, "E20.14.57.0", {"start": v(29.74, -42.78) * mm, "mid": v(30.04, -42.56) * mm, "end": v(30.35, -42.35) * mm});
            skArc(sketch, "E20.1.58.0", {"start": v(30.35, -42.35) * mm, "mid": v(30.64, -42.13) * mm, "end": v(30.93, -41.92) * mm});
            skLineSegment(sketch, "E20.4.58.0", {"start": v(29.47, -39.88) * mm, "end": v(30.93, -41.92) * mm});
            skArc(sketch, "E20.7.58.0", {"start": v(29.47, -39.88) * mm, "mid": v(30.18, -39.35) * mm, "end": v(30.88, -38.8) * mm});
            skLineSegment(sketch, "E20.11.58.0", {"start": v(30.88, -38.8) * mm, "end": v(32.47, -40.74) * mm});
            skArc(sketch, "E20.14.58.0", {"start": v(32.47, -40.74) * mm, "mid": v(32.76, -40.5) * mm, "end": v(33.05, -40.27) * mm});
            skArc(sketch, "E20.1.59.0", {"start": v(33.05, -40.27) * mm, "mid": v(33.33, -40.04) * mm, "end": v(33.6, -39.8) * mm});
            skLineSegment(sketch, "E20.4.59.0", {"start": v(32.02, -37.87) * mm, "end": v(33.6, -39.8) * mm});
            skArc(sketch, "E20.7.59.0", {"start": v(32.02, -37.87) * mm, "mid": v(32.69, -37.29) * mm, "end": v(33.35, -36.7) * mm});
            skLineSegment(sketch, "E20.11.59.0", {"start": v(33.35, -36.7) * mm, "end": v(35.07, -38.53) * mm});
            skArc(sketch, "E20.14.59.0", {"start": v(35.07, -38.53) * mm, "mid": v(35.34, -38.28) * mm, "end": v(35.61, -38.02) * mm});
            skArc(sketch, "E20.1.60.0", {"start": v(35.61, -38.02) * mm, "mid": v(35.88, -37.77) * mm, "end": v(36.14, -37.52) * mm});
            skLineSegment(sketch, "E20.4.60.0", {"start": v(34.43, -35.7) * mm, "end": v(36.14, -37.52) * mm});
            skArc(sketch, "E20.7.60.0", {"start": v(34.43, -35.7) * mm, "mid": v(35.06, -35.07) * mm, "end": v(35.68, -34.44) * mm});
            skLineSegment(sketch, "E20.11.60.0", {"start": v(35.68, -34.44) * mm, "end": v(37.51, -36.15) * mm});
            skArc(sketch, "E20.14.60.0", {"start": v(37.51, -36.15) * mm, "mid": v(37.77, -35.88) * mm, "end": v(38.02, -35.61) * mm});
            skArc(sketch, "E20.1.61.0", {"start": v(38.02, -35.61) * mm, "mid": v(38.27, -35.35) * mm, "end": v(38.52, -35.08) * mm});
            skLineSegment(sketch, "E20.4.61.0", {"start": v(36.69, -33.36) * mm, "end": v(38.52, -35.08) * mm});
            skArc(sketch, "E20.7.61.0", {"start": v(36.69, -33.36) * mm, "mid": v(37.28, -32.7) * mm, "end": v(37.86, -32.03) * mm});
            skLineSegment(sketch, "E20.11.61.0", {"start": v(37.86, -32.03) * mm, "end": v(39.8, -33.62) * mm});
            skArc(sketch, "E20.14.61.0", {"start": v(39.8, -33.62) * mm, "mid": v(40.03, -33.34) * mm, "end": v(40.27, -33.05) * mm});
            skArc(sketch, "E20.1.62.0", {"start": v(40.27, -33.05) * mm, "mid": v(40.5, -32.77) * mm, "end": v(40.73, -32.49) * mm});
            skLineSegment(sketch, "E20.4.62.0", {"start": v(38.79, -30.9) * mm, "end": v(40.73, -32.49) * mm});
            skArc(sketch, "E20.7.62.0", {"start": v(38.79, -30.9) * mm, "mid": v(39.34, -30.2) * mm, "end": v(39.87, -29.48) * mm});
            skLineSegment(sketch, "E20.11.62.0", {"start": v(39.87, -29.48) * mm, "end": v(41.9, -30.95) * mm});
            skArc(sketch, "E20.14.62.0", {"start": v(41.9, -30.95) * mm, "mid": v(42.13, -30.65) * mm, "end": v(42.35, -30.35) * mm});
            skArc(sketch, "E20.1.63.0", {"start": v(42.35, -30.35) * mm, "mid": v(42.56, -30.05) * mm, "end": v(42.77, -29.75) * mm});
            skLineSegment(sketch, "E20.4.63.0", {"start": v(40.73, -28.3) * mm, "end": v(42.77, -29.75) * mm});
            skArc(sketch, "E20.7.63.0", {"start": v(40.73, -28.3) * mm, "mid": v(41.23, -27.56) * mm, "end": v(41.71, -26.81) * mm});
            skLineSegment(sketch, "E20.11.63.0", {"start": v(41.71, -26.81) * mm, "end": v(43.84, -28.14) * mm});
            skArc(sketch, "E20.14.63.0", {"start": v(43.84, -28.14) * mm, "mid": v(44.04, -27.83) * mm, "end": v(44.24, -27.51) * mm});
            skArc(sketch, "E20.1.64.0", {"start": v(44.24, -27.51) * mm, "mid": v(44.43, -27.2) * mm, "end": v(44.62, -26.9) * mm});
            skLineSegment(sketch, "E20.4.64.0", {"start": v(42.49, -25.57) * mm, "end": v(44.62, -26.9) * mm});
            skArc(sketch, "E20.7.64.0", {"start": v(42.49, -25.57) * mm, "mid": v(42.94, -24.8) * mm, "end": v(43.38, -24.03) * mm});
            skLineSegment(sketch, "E20.11.64.0", {"start": v(43.38, -24.03) * mm, "end": v(45.6, -25.21) * mm});
            skArc(sketch, "E20.14.64.0", {"start": v(45.6, -25.21) * mm, "mid": v(45.77, -24.89) * mm, "end": v(45.95, -24.56) * mm});
            skArc(sketch, "E20.1.65.0", {"start": v(45.95, -24.56) * mm, "mid": v(46.12, -24.24) * mm, "end": v(46.28, -23.92) * mm});
            skLineSegment(sketch, "E20.4.65.0", {"start": v(44.07, -22.73) * mm, "end": v(46.28, -23.92) * mm});
            skArc(sketch, "E20.7.65.0", {"start": v(44.07, -22.73) * mm, "mid": v(44.47, -21.94) * mm, "end": v(44.86, -21.14) * mm});
            skLineSegment(sketch, "E20.11.65.0", {"start": v(44.86, -21.14) * mm, "end": v(47.14, -22.18) * mm});
            skArc(sketch, "E20.14.65.0", {"start": v(47.14, -22.18) * mm, "mid": v(47.3, -21.84) * mm, "end": v(47.45, -21.5) * mm});
            skArc(sketch, "E20.1.66.0", {"start": v(47.45, -21.5) * mm, "mid": v(47.6, -21.17) * mm, "end": v(47.75, -20.84) * mm});
            skLineSegment(sketch, "E20.4.66.0", {"start": v(45.46, -19.8) * mm, "end": v(47.75, -20.84) * mm});
            skArc(sketch, "E20.7.66.0", {"start": v(45.46, -19.8) * mm, "mid": v(45.81, -18.98) * mm, "end": v(46.14, -18.16) * mm});
            skLineSegment(sketch, "E20.11.66.0", {"start": v(46.14, -18.16) * mm, "end": v(48.5, -19.04) * mm});
            skArc(sketch, "E20.14.66.0", {"start": v(48.5, -19.04) * mm, "mid": v(48.63, -18.7) * mm, "end": v(48.76, -18.35) * mm});
            skArc(sketch, "E20.1.67.0", {"start": v(48.76, -18.35) * mm, "mid": v(48.88, -18.01) * mm, "end": v(49, -17.67) * mm});
            skLineSegment(sketch, "E20.4.67.0", {"start": v(46.66, -16.79) * mm, "end": v(49, -17.67) * mm});
            skArc(sketch, "E20.7.67.0", {"start": v(46.66, -16.79) * mm, "mid": v(46.95, -15.95) * mm, "end": v(47.23, -15.1) * mm});
            skLineSegment(sketch, "E20.11.67.0", {"start": v(47.23, -15.1) * mm, "end": v(49.63, -15.83) * mm});
            skArc(sketch, "E20.14.67.0", {"start": v(49.63, -15.83) * mm, "mid": v(49.74, -15.48) * mm, "end": v(49.85, -15.12) * mm});
            skArc(sketch, "E20.1.68.0", {"start": v(49.85, -15.12) * mm, "mid": v(49.96, -14.77) * mm, "end": v(50.06, -14.43) * mm});
            skLineSegment(sketch, "E20.4.68.0", {"start": v(47.66, -13.7) * mm, "end": v(50.06, -14.43) * mm});
            skArc(sketch, "E20.7.68.0", {"start": v(47.66, -13.7) * mm, "mid": v(47.9, -12.84) * mm, "end": v(48.12, -11.98) * mm});
            skLineSegment(sketch, "E20.11.68.0", {"start": v(48.12, -11.98) * mm, "end": v(50.56, -12.55) * mm});
            skArc(sketch, "E20.14.68.0", {"start": v(50.56, -12.55) * mm, "mid": v(50.65, -12.2) * mm, "end": v(50.74, -11.83) * mm});
            skArc(sketch, "E20.1.69.0", {"start": v(50.74, -11.83) * mm, "mid": v(50.82, -11.48) * mm, "end": v(50.9, -11.12) * mm});
            skLineSegment(sketch, "E20.4.69.0", {"start": v(48.45, -10.55) * mm, "end": v(50.9, -11.12) * mm});
            skArc(sketch, "E20.7.69.0", {"start": v(48.45, -10.55) * mm, "mid": v(48.63, -9.68) * mm, "end": v(48.8, -8.8) * mm});
            skLineSegment(sketch, "E20.11.69.0", {"start": v(48.8, -8.8) * mm, "end": v(51.27, -9.22) * mm});
            skArc(sketch, "E20.14.69.0", {"start": v(51.27, -9.22) * mm, "mid": v(51.34, -8.85) * mm, "end": v(51.4, -8.49) * mm});
            skArc(sketch, "E20.1.70.0", {"start": v(51.4, -8.49) * mm, "mid": v(51.46, -8.13) * mm, "end": v(51.51, -7.77) * mm});
            skLineSegment(sketch, "E20.4.70.0", {"start": v(49.04, -7.36) * mm, "end": v(51.51, -7.77) * mm});
            skArc(sketch, "E20.7.70.0", {"start": v(49.04, -7.36) * mm, "mid": v(49.16, -6.48) * mm, "end": v(49.27, -5.6) * mm});
            skLineSegment(sketch, "E20.11.70.0", {"start": v(49.27, -5.6) * mm, "end": v(51.77, -5.85) * mm});
            skArc(sketch, "E20.14.70.0", {"start": v(51.77, -5.85) * mm, "mid": v(51.8, -5.48) * mm, "end": v(51.85, -5.1) * mm});
            skArc(sketch, "E20.1.71.0", {"start": v(51.85, -5.1) * mm, "mid": v(51.88, -4.74) * mm, "end": v(51.91, -4.38) * mm});
            skLineSegment(sketch, "E20.4.71.0", {"start": v(49.42, -4.14) * mm, "end": v(51.91, -4.38) * mm});
            skArc(sketch, "E20.7.71.0", {"start": v(49.42, -4.14) * mm, "mid": v(49.48, -3.25) * mm, "end": v(49.53, -2.36) * mm});
            skLineSegment(sketch, "E20.11.71.0", {"start": v(49.53, -2.36) * mm, "end": v(52.04, -2.45) * mm});
            skArc(sketch, "E20.14.71.0", {"start": v(52.04, -2.45) * mm, "mid": v(52.06, -2.08) * mm, "end": v(52.07, -1.7) * mm});
            skArc(sketch, "E20.1.72.0", {"start": v(52.07, -1.7) * mm, "mid": v(52.08, -1.34) * mm, "end": v(52.09, -0.98) * mm});
            skLineSegment(sketch, "E20.4.72.0", {"start": v(49.58, -0.9) * mm, "end": v(52.09, -0.98) * mm});
            skArc(sketch, "E20.7.72.0", {"start": v(49.58, -0.9) * mm, "mid": v(49.59, 0) * mm, "end": v(49.58, 0.88) * mm});
            skLineSegment(sketch, "E20.11.72.0", {"start": v(49.58, 0.88) * mm, "end": v(52.09, 0.96) * mm});
            skArc(sketch, "E20.14.72.0", {"start": v(52.09, 0.96) * mm, "mid": v(52.08, 1.33) * mm, "end": v(52.07, 1.7) * mm});
            skArc(sketch, "E20.1.73.0", {"start": v(52.07, 1.7) * mm, "mid": v(52.06, 2.07) * mm, "end": v(52.04, 2.43) * mm});
            skLineSegment(sketch, "E20.4.73.0", {"start": v(49.53, 2.35) * mm, "end": v(52.04, 2.43) * mm});
            skArc(sketch, "E20.7.73.0", {"start": v(49.53, 2.35) * mm, "mid": v(49.48, 3.24) * mm, "end": v(49.42, 4.12) * mm});
            skLineSegment(sketch, "E20.11.73.0", {"start": v(49.42, 4.12) * mm, "end": v(51.91, 4.37) * mm});
            skArc(sketch, "E20.14.73.0", {"start": v(51.91, 4.37) * mm, "mid": v(51.88, 4.74) * mm, "end": v(51.85, 5.1) * mm});
            skArc(sketch, "E20.1.74.0", {"start": v(51.85, 5.1) * mm, "mid": v(51.8, 5.47) * mm, "end": v(51.77, 5.83) * mm});
            skLineSegment(sketch, "E20.4.74.0", {"start": v(49.27, 5.58) * mm, "end": v(51.77, 5.83) * mm});
            skArc(sketch, "E20.7.74.0", {"start": v(49.27, 5.58) * mm, "mid": v(49.17, 6.46) * mm, "end": v(49.04, 7.34) * mm});
            skLineSegment(sketch, "E20.11.74.0", {"start": v(49.04, 7.34) * mm, "end": v(51.52, 7.75) * mm});
            skArc(sketch, "E20.14.74.0", {"start": v(51.52, 7.75) * mm, "mid": v(51.46, 8.12) * mm, "end": v(51.4, 8.49) * mm});
            skArc(sketch, "E20.1.75.0", {"start": v(51.4, 8.49) * mm, "mid": v(51.34, 8.84) * mm, "end": v(51.28, 9.2) * mm});
            skLineSegment(sketch, "E20.4.75.0", {"start": v(48.8, 8.8) * mm, "end": v(51.28, 9.2) * mm});
            skArc(sketch, "E20.7.75.0", {"start": v(48.8, 8.8) * mm, "mid": v(48.64, 9.67) * mm, "end": v(48.46, 10.54) * mm});
            skLineSegment(sketch, "E20.11.75.0", {"start": v(48.46, 10.54) * mm, "end": v(50.9, 11.1) * mm});
            skArc(sketch, "E20.14.75.0", {"start": v(50.9, 11.1) * mm, "mid": v(50.82, 11.47) * mm, "end": v(50.74, 11.83) * mm});
            skArc(sketch, "E20.1.76.0", {"start": v(50.74, 11.83) * mm, "mid": v(50.65, 12.18) * mm, "end": v(50.57, 12.54) * mm});
            skLineSegment(sketch, "E20.4.76.0", {"start": v(48.12, 11.97) * mm, "end": v(50.57, 12.54) * mm});
            skArc(sketch, "E20.7.76.0", {"start": v(48.12, 11.97) * mm, "mid": v(47.9, 12.83) * mm, "end": v(47.66, 13.68) * mm});
            skLineSegment(sketch, "E20.11.76.0", {"start": v(47.66, 13.68) * mm, "end": v(50.06, 14.41) * mm});
            skArc(sketch, "E20.14.76.0", {"start": v(50.06, 14.41) * mm, "mid": v(49.96, 14.77) * mm, "end": v(49.85, 15.12) * mm});
            skArc(sketch, "E20.1.77.0", {"start": v(49.85, 15.12) * mm, "mid": v(49.75, 15.47) * mm, "end": v(49.64, 15.82) * mm});
            skLineSegment(sketch, "E20.4.77.0", {"start": v(47.24, 15.09) * mm, "end": v(49.64, 15.82) * mm});
            skArc(sketch, "E20.7.77.0", {"start": v(47.24, 15.09) * mm, "mid": v(46.96, 15.93) * mm, "end": v(46.67, 16.77) * mm});
            skLineSegment(sketch, "E20.11.77.0", {"start": v(46.67, 16.77) * mm, "end": v(49.01, 17.65) * mm});
            skArc(sketch, "E20.14.77.0", {"start": v(49.01, 17.65) * mm, "mid": v(48.89, 18) * mm, "end": v(48.76, 18.35) * mm});
            skArc(sketch, "E20.1.78.0", {"start": v(48.76, 18.35) * mm, "mid": v(48.63, 18.7) * mm, "end": v(48.5, 19.03) * mm});
            skLineSegment(sketch, "E20.4.78.0", {"start": v(46.15, 18.15) * mm, "end": v(48.5, 19.03) * mm});
            skArc(sketch, "E20.7.78.0", {"start": v(46.15, 18.15) * mm, "mid": v(45.82, 18.97) * mm, "end": v(45.47, 19.79) * mm});
            skLineSegment(sketch, "E20.11.78.0", {"start": v(45.47, 19.79) * mm, "end": v(47.76, 20.82) * mm});
            skArc(sketch, "E20.14.78.0", {"start": v(47.76, 20.82) * mm, "mid": v(47.6, 21.16) * mm, "end": v(47.45, 21.5) * mm});
            skArc(sketch, "E20.1.79.0", {"start": v(47.45, 21.5) * mm, "mid": v(47.3, 21.83) * mm, "end": v(47.15, 22.16) * mm});
            skLineSegment(sketch, "E20.4.79.0", {"start": v(44.86, 21.13) * mm, "end": v(47.15, 22.16) * mm});
            skArc(sketch, "E20.7.79.0", {"start": v(44.86, 21.13) * mm, "mid": v(44.48, 21.93) * mm, "end": v(44.08, 22.72) * mm});
            skLineSegment(sketch, "E20.11.79.0", {"start": v(44.08, 22.72) * mm, "end": v(46.3, 23.9) * mm});
            skArc(sketch, "E20.14.79.0", {"start": v(46.3, 23.9) * mm, "mid": v(46.12, 24.23) * mm, "end": v(45.95, 24.56) * mm});
            skArc(sketch, "E20.1.80.0", {"start": v(45.95, 24.56) * mm, "mid": v(45.77, 24.88) * mm, "end": v(45.6, 25.2) * mm});
            skLineSegment(sketch, "E20.4.80.0", {"start": v(43.39, 24.01) * mm, "end": v(45.6, 25.2) * mm});
            skArc(sketch, "E20.7.80.0", {"start": v(43.39, 24.01) * mm, "mid": v(42.95, 24.79) * mm, "end": v(42.5, 25.55) * mm});
            skLineSegment(sketch, "E20.11.80.0", {"start": v(42.5, 25.55) * mm, "end": v(44.63, 26.88) * mm});
            skArc(sketch, "E20.14.80.0", {"start": v(44.63, 26.88) * mm, "mid": v(44.44, 27.2) * mm, "end": v(44.24, 27.51) * mm});
            skArc(sketch, "E20.1.81.0", {"start": v(44.24, 27.51) * mm, "mid": v(44.05, 27.82) * mm, "end": v(43.85, 28.13) * mm});
            skLineSegment(sketch, "E20.4.81.0", {"start": v(41.72, 26.8) * mm, "end": v(43.85, 28.13) * mm});
            skArc(sketch, "E20.7.81.0", {"start": v(41.72, 26.8) * mm, "mid": v(41.24, 27.54) * mm, "end": v(40.74, 28.28) * mm});
            skLineSegment(sketch, "E20.11.81.0", {"start": v(40.74, 28.28) * mm, "end": v(42.78, 29.74) * mm});
            skArc(sketch, "E20.14.81.0", {"start": v(42.78, 29.74) * mm, "mid": v(42.56, 30.04) * mm, "end": v(42.35, 30.35) * mm});
            skArc(sketch, "E20.1.82.0", {"start": v(42.35, 30.35) * mm, "mid": v(42.13, 30.64) * mm, "end": v(41.92, 30.93) * mm});
            skLineSegment(sketch, "E20.4.82.0", {"start": v(39.88, 29.47) * mm, "end": v(41.92, 30.93) * mm});
            skArc(sketch, "E20.7.82.0", {"start": v(39.88, 29.47) * mm, "mid": v(39.35, 30.18) * mm, "end": v(38.8, 30.88) * mm});
            skLineSegment(sketch, "E20.11.82.0", {"start": v(38.8, 30.88) * mm, "end": v(40.74, 32.47) * mm});
            skArc(sketch, "E20.14.82.0", {"start": v(40.74, 32.47) * mm, "mid": v(40.5, 32.76) * mm, "end": v(40.27, 33.05) * mm});
            skArc(sketch, "E20.1.83.0", {"start": v(40.27, 33.05) * mm, "mid": v(40.04, 33.33) * mm, "end": v(39.8, 33.6) * mm});
            skLineSegment(sketch, "E20.4.83.0", {"start": v(37.87, 32.02) * mm, "end": v(39.8, 33.6) * mm});
            skArc(sketch, "E20.7.83.0", {"start": v(37.87, 32.02) * mm, "mid": v(37.29, 32.69) * mm, "end": v(36.7, 33.35) * mm});
            skLineSegment(sketch, "E20.11.83.0", {"start": v(36.7, 33.35) * mm, "end": v(38.53, 35.07) * mm});
            skArc(sketch, "E20.14.83.0", {"start": v(38.53, 35.07) * mm, "mid": v(38.28, 35.34) * mm, "end": v(38.02, 35.61) * mm});
            skArc(sketch, "E20.1.84.0", {"start": v(38.02, 35.61) * mm, "mid": v(37.77, 35.88) * mm, "end": v(37.52, 36.14) * mm});
            skLineSegment(sketch, "E20.4.84.0", {"start": v(35.7, 34.43) * mm, "end": v(37.52, 36.14) * mm});
            skArc(sketch, "E20.7.84.0", {"start": v(35.7, 34.43) * mm, "mid": v(35.07, 35.06) * mm, "end": v(34.44, 35.68) * mm});
            skLineSegment(sketch, "E20.11.84.0", {"start": v(34.44, 35.68) * mm, "end": v(36.15, 37.51) * mm});
            skArc(sketch, "E20.14.84.0", {"start": v(36.15, 37.51) * mm, "mid": v(35.88, 37.77) * mm, "end": v(35.61, 38.02) * mm});
            skArc(sketch, "E20.1.85.0", {"start": v(35.61, 38.02) * mm, "mid": v(35.35, 38.27) * mm, "end": v(35.08, 38.52) * mm});
            skLineSegment(sketch, "E20.4.85.0", {"start": v(33.36, 36.69) * mm, "end": v(35.08, 38.52) * mm});
            skArc(sketch, "E20.7.85.0", {"start": v(33.36, 36.69) * mm, "mid": v(32.7, 37.28) * mm, "end": v(32.03, 37.86) * mm});
            skLineSegment(sketch, "E20.11.85.0", {"start": v(32.03, 37.86) * mm, "end": v(33.62, 39.8) * mm});
            skArc(sketch, "E20.14.85.0", {"start": v(33.62, 39.8) * mm, "mid": v(33.34, 40.03) * mm, "end": v(33.05, 40.27) * mm});
            skArc(sketch, "E20.1.86.0", {"start": v(33.05, 40.27) * mm, "mid": v(32.77, 40.5) * mm, "end": v(32.49, 40.73) * mm});
            skLineSegment(sketch, "E20.4.86.0", {"start": v(30.9, 38.79) * mm, "end": v(32.49, 40.73) * mm});
            skArc(sketch, "E20.7.86.0", {"start": v(30.9, 38.79) * mm, "mid": v(30.2, 39.34) * mm, "end": v(29.48, 39.87) * mm});
            skLineSegment(sketch, "E20.11.86.0", {"start": v(29.48, 39.87) * mm, "end": v(30.95, 41.9) * mm});
            skArc(sketch, "E20.14.86.0", {"start": v(30.95, 41.9) * mm, "mid": v(30.65, 42.13) * mm, "end": v(30.35, 42.35) * mm});
            skArc(sketch, "E20.1.87.0", {"start": v(30.35, 42.35) * mm, "mid": v(30.05, 42.56) * mm, "end": v(29.75, 42.77) * mm});
            skLineSegment(sketch, "E20.4.87.0", {"start": v(28.3, 40.73) * mm, "end": v(29.75, 42.77) * mm});
            skArc(sketch, "E20.7.87.0", {"start": v(28.3, 40.73) * mm, "mid": v(27.56, 41.23) * mm, "end": v(26.81, 41.71) * mm});
            skLineSegment(sketch, "E20.11.87.0", {"start": v(26.81, 41.71) * mm, "end": v(28.14, 43.84) * mm});
            skArc(sketch, "E20.14.87.0", {"start": v(28.14, 43.84) * mm, "mid": v(27.83, 44.04) * mm, "end": v(27.51, 44.24) * mm});
            skArc(sketch, "E20.1.88.0", {"start": v(27.51, 44.24) * mm, "mid": v(27.2, 44.43) * mm, "end": v(26.9, 44.62) * mm});
            skLineSegment(sketch, "E20.4.88.0", {"start": v(25.57, 42.49) * mm, "end": v(26.9, 44.62) * mm});
            skArc(sketch, "E20.7.88.0", {"start": v(25.57, 42.49) * mm, "mid": v(24.8, 42.94) * mm, "end": v(24.03, 43.38) * mm});
            skLineSegment(sketch, "E20.11.88.0", {"start": v(24.03, 43.38) * mm, "end": v(25.21, 45.6) * mm});
            skArc(sketch, "E20.14.88.0", {"start": v(25.21, 45.6) * mm, "mid": v(24.89, 45.77) * mm, "end": v(24.56, 45.95) * mm});
            skArc(sketch, "E20.1.89.0", {"start": v(24.56, 45.95) * mm, "mid": v(24.24, 46.12) * mm, "end": v(23.92, 46.28) * mm});
            skLineSegment(sketch, "E20.4.89.0", {"start": v(22.73, 44.07) * mm, "end": v(23.92, 46.28) * mm});
            skArc(sketch, "E20.7.89.0", {"start": v(22.73, 44.07) * mm, "mid": v(21.94, 44.47) * mm, "end": v(21.14, 44.86) * mm});
            skLineSegment(sketch, "E20.11.89.0", {"start": v(21.14, 44.86) * mm, "end": v(22.18, 47.14) * mm});
            skArc(sketch, "E20.14.89.0", {"start": v(22.18, 47.14) * mm, "mid": v(21.84, 47.3) * mm, "end": v(21.5, 47.45) * mm});
            skArc(sketch, "E20.1.90.0", {"start": v(21.5, 47.45) * mm, "mid": v(21.17, 47.6) * mm, "end": v(20.84, 47.75) * mm});
            skLineSegment(sketch, "E20.4.90.0", {"start": v(19.8, 45.46) * mm, "end": v(20.84, 47.75) * mm});
            skArc(sketch, "E20.7.90.0", {"start": v(19.8, 45.46) * mm, "mid": v(18.98, 45.81) * mm, "end": v(18.16, 46.14) * mm});
            skLineSegment(sketch, "E20.11.90.0", {"start": v(18.16, 46.14) * mm, "end": v(19.04, 48.5) * mm});
            skArc(sketch, "E20.14.90.0", {"start": v(19.04, 48.5) * mm, "mid": v(18.7, 48.63) * mm, "end": v(18.35, 48.76) * mm});
            skArc(sketch, "E20.1.91.0", {"start": v(18.35, 48.76) * mm, "mid": v(18.01, 48.88) * mm, "end": v(17.67, 49) * mm});
            skLineSegment(sketch, "E20.4.91.0", {"start": v(16.79, 46.66) * mm, "end": v(17.67, 49) * mm});
            skArc(sketch, "E20.7.91.0", {"start": v(16.79, 46.66) * mm, "mid": v(15.95, 46.95) * mm, "end": v(15.1, 47.23) * mm});
            skLineSegment(sketch, "E20.11.91.0", {"start": v(15.1, 47.23) * mm, "end": v(15.83, 49.63) * mm});
            skArc(sketch, "E20.14.91.0", {"start": v(15.83, 49.63) * mm, "mid": v(15.48, 49.74) * mm, "end": v(15.12, 49.85) * mm});
            skArc(sketch, "E20.1.92.0", {"start": v(15.12, 49.85) * mm, "mid": v(14.77, 49.96) * mm, "end": v(14.43, 50.06) * mm});
            skLineSegment(sketch, "E20.4.92.0", {"start": v(13.7, 47.66) * mm, "end": v(14.43, 50.06) * mm});
            skArc(sketch, "E20.7.92.0", {"start": v(13.7, 47.66) * mm, "mid": v(12.84, 47.9) * mm, "end": v(11.98, 48.12) * mm});
            skLineSegment(sketch, "E20.11.92.0", {"start": v(11.98, 48.12) * mm, "end": v(12.55, 50.56) * mm});
            skArc(sketch, "E20.14.92.0", {"start": v(12.55, 50.56) * mm, "mid": v(12.2, 50.65) * mm, "end": v(11.83, 50.74) * mm});
            skArc(sketch, "E20.1.93.0", {"start": v(11.83, 50.74) * mm, "mid": v(11.48, 50.82) * mm, "end": v(11.12, 50.9) * mm});
            skLineSegment(sketch, "E20.4.93.0", {"start": v(10.55, 48.45) * mm, "end": v(11.12, 50.9) * mm});
            skArc(sketch, "E20.7.93.0", {"start": v(10.55, 48.45) * mm, "mid": v(9.68, 48.63) * mm, "end": v(8.8, 48.8) * mm});
            skLineSegment(sketch, "E20.11.93.0", {"start": v(8.8, 48.8) * mm, "end": v(9.22, 51.27) * mm});
            skArc(sketch, "E20.14.93.0", {"start": v(9.22, 51.27) * mm, "mid": v(8.85, 51.34) * mm, "end": v(8.49, 51.4) * mm});
            skArc(sketch, "E20.1.94.0", {"start": v(8.49, 51.4) * mm, "mid": v(8.13, 51.46) * mm, "end": v(7.77, 51.51) * mm});
            skLineSegment(sketch, "E20.4.94.0", {"start": v(7.36, 49.04) * mm, "end": v(7.77, 51.51) * mm});
            skArc(sketch, "E20.7.94.0", {"start": v(7.36, 49.04) * mm, "mid": v(6.48, 49.16) * mm, "end": v(5.6, 49.27) * mm});
            skLineSegment(sketch, "E20.11.94.0", {"start": v(5.6, 49.27) * mm, "end": v(5.85, 51.77) * mm});
            skArc(sketch, "E20.14.94.0", {"start": v(5.85, 51.77) * mm, "mid": v(5.48, 51.8) * mm, "end": v(5.1, 51.85) * mm});
            skArc(sketch, "E20.1.95.0", {"start": v(5.1, 51.85) * mm, "mid": v(4.74, 51.88) * mm, "end": v(4.38, 51.91) * mm});
            skLineSegment(sketch, "E20.4.95.0", {"start": v(4.14, 49.42) * mm, "end": v(4.38, 51.91) * mm});
            skArc(sketch, "E20.7.95.0", {"start": v(4.14, 49.42) * mm, "mid": v(3.25, 49.48) * mm, "end": v(2.36, 49.53) * mm});
            skLineSegment(sketch, "E20.11.95.0", {"start": v(2.36, 49.53) * mm, "end": v(2.45, 52.04) * mm});
            skArc(sketch, "E20.14.95.0", {"start": v(2.45, 52.04) * mm, "mid": v(2.08, 52.06) * mm, "end": v(1.7, 52.07) * mm});
            skSolve(sketch);
        }
        {
            var Q0;
            Q0=makeQuery(id+"F3.imprint","IMPRINT",FACE,{"disambiguationData":[TD([[makeQuery(id+"F3.imprint","IMPRINT",EDGE,{"derivedFrom":sQuery(id+"F3.wireOp",EDGE,"E9")}),-1.0]])]});
            var Q1;
            Q1=makeQuery(id+"F3.imprint","IMPRINT",FACE,{"disambiguationData":[TD([[makeQuery(id+"F3.imprint","IMPRINT",EDGE,{"derivedFrom":sQuery(id+"F3.wireOp",EDGE,"E10")}),1.0]])]});
            extrude(context, id + "F4", {"entities" : qUnion([Q0, Q1]), "depth" : 6.35 * mm});
        }
        {
            var Q0;
            Q0=makeQuery(id+"F2.opExtrude","CAP_FACE",FACE,{"disambiguationData":[OSD([sQuery(id+"F0.wireOp",EDGE,"E0")])],"isStart":false});
            var sketch = newSketch(context, id + "F5", { "sketchPlane" : qUnion([Q0])});
            skCircle(sketch, "E21", {"center": v(0, 0) * mm, "radius": 9.53 * mm});
            skLineSegment(sketch, "E22", {"start": v(0, 41.28) * mm, "end": v(0, 0) * mm});
            skArc(sketch, "E23", {"start": v(-11.43, 15.24) * mm, "mid": v(0, -19.05) * mm, "end": v(11.43, 15.24) * mm});
            skLineSegment(sketch, "E24", {"start": v(-6.35, 25.4) * mm, "end": v(-6.35, 41.28) * mm});
            skLineSegment(sketch, "E25", {"start": v(6.35, 25.4) * mm, "end": v(6.35, 41.28) * mm});
            skArc(sketch, "E26", {"start": v(6.35, 41.28) * mm, "mid": v(0, 47.63) * mm, "end": v(-6.35, 41.28) * mm});
            skPoint(sketch, "E27.visualSharp", {"position": v(-6.35, 17.96) * mm});
            skArc(sketch, "E27.filletArc", {"start": v(-11.43, 15.24) * mm, "mid": v(-7.7, 19.72) * mm, "end": v(-6.35, 25.4) * mm});
            skPoint(sketch, "E28.visualSharp", {"position": v(6.35, 17.96) * mm});
            skArc(sketch, "E28.filletArc", {"start": v(6.35, 25.4) * mm, "mid": v(7.7, 19.72) * mm, "end": v(11.43, 15.24) * mm});
            skLineSegment(sketch, "E29", {"start": v(0, 31.75) * mm, "end": v(0, 50.8) * mm});
            skLineSegment(sketch, "E30.1.0", {"start": v(-25.17, -7.2) * mm, "end": v(-38.92, -15.14) * mm});
            skArc(sketch, "E30.1.1", {"start": v(-38.92, -15.14) * mm, "mid": v(-41.24, -23.81) * mm, "end": v(-32.57, -26.14) * mm});
            skLineSegment(sketch, "E30.1.2", {"start": v(-18.82, -18.2) * mm, "end": v(-32.57, -26.14) * mm});
            skArc(sketch, "E30.1.3", {"start": v(-7.48, -17.52) * mm, "mid": v(-13.23, -16.52) * mm, "end": v(-18.82, -18.2) * mm});
            skArc(sketch, "E30.1.4", {"start": v(-25.17, -7.2) * mm, "mid": v(-20.92, -3.2) * mm, "end": v(-18.91, 2.28) * mm});
            skLineSegment(sketch, "E30.2.0", {"start": v(18.82, -18.2) * mm, "end": v(32.57, -26.14) * mm});
            skArc(sketch, "E30.2.1", {"start": v(32.57, -26.14) * mm, "mid": v(41.24, -23.81) * mm, "end": v(38.92, -15.14) * mm});
            skLineSegment(sketch, "E30.2.2", {"start": v(25.17, -7.2) * mm, "end": v(38.92, -15.14) * mm});
            skArc(sketch, "E30.2.3", {"start": v(18.91, 2.28) * mm, "mid": v(20.92, -3.2) * mm, "end": v(25.17, -7.2) * mm});
            skArc(sketch, "E30.2.4", {"start": v(18.82, -18.2) * mm, "mid": v(13.23, -16.52) * mm, "end": v(7.48, -17.52) * mm});
            skSolve(sketch);
        }
        {
            var Q0;
            Q0=makeQuery(id+"F5.imprint","IMPRINT",FACE,{"disambiguationData":[TD([[makeQuery(id+"F5.imprint","IMPRINT",EDGE,{"derivedFrom":sQuery(id+"F5.wireOp",EDGE,"E30.1.0")}),1.0]])]});
            var Q1;
            Q1=makeQuery(id+"F5.imprint","IMPRINT",FACE,{"disambiguationData":[TD([[makeQuery(id+"F5.imprint","IMPRINT",EDGE,{"derivedFrom":sQuery(id+"F5.wireOp",EDGE,"E21")}),-1.0]])]});
            var Q2;
            Q2=makeQuery(id+"F5.imprint","IMPRINT",FACE,{"disambiguationData":[TD([[makeQuery(id+"F5.imprint","IMPRINT",EDGE,{"derivedFrom":sQuery(id+"F5.wireOp",EDGE,"E30.2.0")}),1.0]])]});
            extrude(context, id + "F6", {"entities" : qUnion([Q0, Q1, Q2]), "oppositeDirection" : true, "depth" : 6.35 * mm});
        }
        {
            var Q0;
            Q0=makeQuery(id+"F6.opExtrude","CAP_FACE",FACE,{"disambiguationData":[OSD([sQuery(id+"F5.wireOp",EDGE,"E21"),sQuery(id+"F5.wireOp",EDGE,"E23"),sQuery(id+"F5.wireOp",EDGE,"E24"),sQuery(id+"F5.wireOp",EDGE,"E25"),sQuery(id+"F5.wireOp",EDGE,"E26"),sQuery(id+"F5.wireOp",EDGE,"E27.filletArc"),sQuery(id+"F5.wireOp",EDGE,"E28.filletArc"),sQuery(id+"F5.wireOp",EDGE,"E30.1.0"),sQuery(id+"F5.wireOp",EDGE,"E30.1.1"),sQuery(id+"F5.wireOp",EDGE,"E30.1.2"),sQuery(id+"F5.wireOp",EDGE,"E30.1.3"),sQuery(id+"F5.wireOp",EDGE,"E30.1.4"),sQuery(id+"F5.wireOp",EDGE,"E30.2.0"),sQuery(id+"F5.wireOp",EDGE,"E30.2.1"),sQuery(id+"F5.wireOp",EDGE,"E30.2.2"),sQuery(id+"F5.wireOp",EDGE,"E30.2.3"),sQuery(id+"F5.wireOp",EDGE,"E30.2.4")])],"isStart":false});
            var sketch = newSketch(context, id + "F7", { "sketchPlane" : qUnion([Q0])});
            skCircle(sketch, "E31", {"center": v(0, -41.28) * mm, "radius": 9.53 * mm, "construction": true});
            skLineSegment(sketch, "E32", {"start": v(0, -41.28) * mm, "end": v(-2.1, -29.31) * mm, "construction": true});
            skLineSegment(sketch, "E33", {"start": v(0, -41.28) * mm, "end": v(2.06, -29.6) * mm, "construction": true});
            skLineSegment(sketch, "E34", {"start": v(1.1, -30.99) * mm, "end": v(0.92, -33.45) * mm});
            skLineSegment(sketch, "E35", {"start": v(-0.96, -33.46) * mm, "end": v(-1.03, -30.98) * mm});
            skArc(sketch, "E36", {"start": v(1.8, -31.09) * mm, "mid": v(1.45, -31.03) * mm, "end": v(1.1, -30.99) * mm});
            skArc(sketch, "E37", {"start": v(-1.03, -30.98) * mm, "mid": v(-1.41, -31.03) * mm, "end": v(-1.8, -31.09) * mm});
            skArc(sketch, "E38", {"start": v(0.92, -33.45) * mm, "mid": v(-0.02, -33.4) * mm, "end": v(-0.96, -33.46) * mm});
            skLineSegment(sketch, "E39", {"start": v(0, -41.28) * mm, "end": v(0, -36.88) * mm, "construction": true});
            skArc(sketch, "E40.1.0", {"start": v(-1.8, -31.09) * mm, "mid": v(-2.14, -31.15) * mm, "end": v(-2.48, -31.23) * mm});
            skLineSegment(sketch, "E40.1.1", {"start": v(-2.48, -31.23) * mm, "end": v(-1.81, -33.6) * mm});
            skArc(sketch, "E40.1.2", {"start": v(-1.81, -33.6) * mm, "mid": v(-2.71, -33.88) * mm, "end": v(-3.57, -34.25) * mm});
            skLineSegment(sketch, "E40.1.3", {"start": v(-3.57, -34.25) * mm, "end": v(-4.49, -31.95) * mm});
            skArc(sketch, "E40.1.4", {"start": v(-4.49, -31.95) * mm, "mid": v(-4.83, -32.13) * mm, "end": v(-5.17, -32.32) * mm});
            skArc(sketch, "E40.2.0", {"start": v(-5.17, -32.32) * mm, "mid": v(-5.47, -32.5) * mm, "end": v(-5.77, -32.69) * mm});
            skLineSegment(sketch, "E40.2.1", {"start": v(-5.77, -32.69) * mm, "end": v(-4.33, -34.7) * mm});
            skArc(sketch, "E40.2.2", {"start": v(-4.33, -34.7) * mm, "mid": v(-5.08, -35.25) * mm, "end": v(-5.76, -35.9) * mm});
            skLineSegment(sketch, "E40.2.3", {"start": v(-5.76, -35.9) * mm, "end": v(-7.4, -34.05) * mm});
            skArc(sketch, "E40.2.4", {"start": v(-7.4, -34.05) * mm, "mid": v(-7.67, -34.33) * mm, "end": v(-7.92, -34.63) * mm});
            skArc(sketch, "E40.3.0", {"start": v(-7.92, -34.63) * mm, "mid": v(-8.14, -34.9) * mm, "end": v(-8.36, -35.18) * mm});
            skLineSegment(sketch, "E40.3.1", {"start": v(-8.36, -35.18) * mm, "end": v(-6.32, -36.57) * mm});
            skArc(sketch, "E40.3.2", {"start": v(-6.32, -36.57) * mm, "mid": v(-6.83, -37.35) * mm, "end": v(-7.25, -38.2) * mm});
            skLineSegment(sketch, "E40.3.3", {"start": v(-7.25, -38.2) * mm, "end": v(-9.43, -37.02) * mm});
            skArc(sketch, "E40.3.4", {"start": v(-9.43, -37.02) * mm, "mid": v(-9.58, -37.38) * mm, "end": v(-9.72, -37.74) * mm});
            skArc(sketch, "E40.4.0", {"start": v(-9.72, -37.74) * mm, "mid": v(-9.83, -38.07) * mm, "end": v(-9.94, -38.4) * mm});
            skLineSegment(sketch, "E40.4.1", {"start": v(-9.94, -38.4) * mm, "end": v(-7.55, -39.01) * mm});
            skArc(sketch, "E40.4.2", {"start": v(-7.55, -39.01) * mm, "mid": v(-7.76, -39.93) * mm, "end": v(-7.87, -40.86) * mm});
            skLineSegment(sketch, "E40.4.3", {"start": v(-7.87, -40.86) * mm, "end": v(-10.32, -40.5) * mm});
            skArc(sketch, "E40.4.4", {"start": v(-10.32, -40.5) * mm, "mid": v(-10.34, -40.89) * mm, "end": v(-10.34, -41.28) * mm});
            skArc(sketch, "E40.5.0", {"start": v(-10.34, -41.28) * mm, "mid": v(-10.34, -41.62) * mm, "end": v(-10.32, -41.97) * mm});
            skLineSegment(sketch, "E40.5.1", {"start": v(-10.32, -41.97) * mm, "end": v(-7.86, -41.73) * mm});
            skArc(sketch, "E40.5.2", {"start": v(-7.86, -41.73) * mm, "mid": v(-7.75, -42.66) * mm, "end": v(-7.53, -43.57) * mm});
            skLineSegment(sketch, "E40.5.3", {"start": v(-7.53, -43.57) * mm, "end": v(-9.96, -44.08) * mm});
            skArc(sketch, "E40.5.4", {"start": v(-9.96, -44.08) * mm, "mid": v(-9.85, -44.45) * mm, "end": v(-9.72, -44.81) * mm});
            skArc(sketch, "E40.6.0", {"start": v(-9.72, -44.81) * mm, "mid": v(-9.6, -45.14) * mm, "end": v(-9.46, -45.46) * mm});
            skLineSegment(sketch, "E40.6.1", {"start": v(-9.46, -45.46) * mm, "end": v(-7.23, -44.4) * mm});
            skArc(sketch, "E40.6.2", {"start": v(-7.23, -44.4) * mm, "mid": v(-6.81, -45.23) * mm, "end": v(-6.3, -46.01) * mm});
            skLineSegment(sketch, "E40.6.3", {"start": v(-6.3, -46.01) * mm, "end": v(-8.4, -47.31) * mm});
            skArc(sketch, "E40.6.4", {"start": v(-8.4, -47.31) * mm, "mid": v(-8.17, -47.62) * mm, "end": v(-7.92, -47.92) * mm});
            skArc(sketch, "E40.7.0", {"start": v(-7.92, -47.92) * mm, "mid": v(-7.7, -48.19) * mm, "end": v(-7.46, -48.44) * mm});
            skLineSegment(sketch, "E40.7.1", {"start": v(-7.46, -48.44) * mm, "end": v(-5.73, -46.68) * mm});
            skArc(sketch, "E40.7.2", {"start": v(-5.73, -46.68) * mm, "mid": v(-5.05, -47.32) * mm, "end": v(-4.3, -47.88) * mm});
            skLineSegment(sketch, "E40.7.3", {"start": v(-4.3, -47.88) * mm, "end": v(-5.83, -49.82) * mm});
            skArc(sketch, "E40.7.4", {"start": v(-5.83, -49.82) * mm, "mid": v(-5.5, -50.03) * mm, "end": v(-5.17, -50.23) * mm});
            skArc(sketch, "E40.8.0", {"start": v(-5.17, -50.23) * mm, "mid": v(-4.87, -50.4) * mm, "end": v(-4.56, -50.56) * mm});
            skLineSegment(sketch, "E40.8.1", {"start": v(-4.56, -50.56) * mm, "end": v(-3.54, -48.31) * mm});
            skArc(sketch, "E40.8.2", {"start": v(-3.54, -48.31) * mm, "mid": v(-2.68, -48.68) * mm, "end": v(-1.78, -48.95) * mm});
            skLineSegment(sketch, "E40.8.3", {"start": v(-1.78, -48.95) * mm, "end": v(-2.55, -51.3) * mm});
            skArc(sketch, "E40.8.4", {"start": v(-2.55, -51.3) * mm, "mid": v(-2.18, -51.39) * mm, "end": v(-1.8, -51.46) * mm});
            skArc(sketch, "E40.9.0", {"start": v(-1.8, -51.46) * mm, "mid": v(-1.45, -51.52) * mm, "end": v(-1.1, -51.56) * mm});
            skLineSegment(sketch, "E40.9.1", {"start": v(-1.1, -51.56) * mm, "end": v(-0.92, -49.1) * mm});
            skArc(sketch, "E40.9.2", {"start": v(-0.92, -49.1) * mm, "mid": v(0.02, -49.15) * mm, "end": v(0.96, -49.1) * mm});
            skLineSegment(sketch, "E40.9.3", {"start": v(0.96, -49.1) * mm, "end": v(1.03, -51.57) * mm});
            skArc(sketch, "E40.9.4", {"start": v(1.03, -51.57) * mm, "mid": v(1.41, -51.52) * mm, "end": v(1.8, -51.46) * mm});
            skArc(sketch, "E40.10.0", {"start": v(1.8, -51.46) * mm, "mid": v(2.14, -51.4) * mm, "end": v(2.48, -51.32) * mm});
            skLineSegment(sketch, "E40.10.1", {"start": v(2.48, -51.32) * mm, "end": v(1.81, -48.94) * mm});
            skArc(sketch, "E40.10.2", {"start": v(1.81, -48.94) * mm, "mid": v(2.71, -48.67) * mm, "end": v(3.57, -48.3) * mm});
            skLineSegment(sketch, "E40.10.3", {"start": v(3.57, -48.3) * mm, "end": v(4.49, -50.6) * mm});
            skArc(sketch, "E40.10.4", {"start": v(4.49, -50.6) * mm, "mid": v(4.83, -50.42) * mm, "end": v(5.17, -50.23) * mm});
            skArc(sketch, "E40.11.0", {"start": v(5.17, -50.23) * mm, "mid": v(5.47, -50.05) * mm, "end": v(5.77, -49.86) * mm});
            skLineSegment(sketch, "E40.11.1", {"start": v(5.77, -49.86) * mm, "end": v(4.33, -47.86) * mm});
            skArc(sketch, "E40.11.2", {"start": v(4.33, -47.86) * mm, "mid": v(5.08, -47.3) * mm, "end": v(5.76, -46.65) * mm});
            skLineSegment(sketch, "E40.11.3", {"start": v(5.76, -46.65) * mm, "end": v(7.4, -48.5) * mm});
            skArc(sketch, "E40.11.4", {"start": v(7.4, -48.5) * mm, "mid": v(7.67, -48.22) * mm, "end": v(7.92, -47.92) * mm});
            skArc(sketch, "E40.12.0", {"start": v(7.92, -47.92) * mm, "mid": v(8.14, -47.65) * mm, "end": v(8.36, -47.37) * mm});
            skLineSegment(sketch, "E40.12.1", {"start": v(8.36, -47.37) * mm, "end": v(6.32, -45.98) * mm});
            skArc(sketch, "E40.12.2", {"start": v(6.32, -45.98) * mm, "mid": v(6.83, -45.2) * mm, "end": v(7.25, -44.36) * mm});
            skLineSegment(sketch, "E40.12.3", {"start": v(7.25, -44.36) * mm, "end": v(9.43, -45.53) * mm});
            skArc(sketch, "E40.12.4", {"start": v(9.43, -45.53) * mm, "mid": v(9.58, -45.17) * mm, "end": v(9.72, -44.81) * mm});
            skArc(sketch, "E40.13.0", {"start": v(9.72, -44.81) * mm, "mid": v(9.83, -44.48) * mm, "end": v(9.94, -44.15) * mm});
            skLineSegment(sketch, "E40.13.1", {"start": v(9.94, -44.15) * mm, "end": v(7.55, -43.54) * mm});
            skArc(sketch, "E40.13.2", {"start": v(7.55, -43.54) * mm, "mid": v(7.76, -42.62) * mm, "end": v(7.87, -41.7) * mm});
            skLineSegment(sketch, "E40.13.3", {"start": v(7.87, -41.7) * mm, "end": v(10.32, -42.05) * mm});
            skArc(sketch, "E40.13.4", {"start": v(10.32, -42.05) * mm, "mid": v(10.34, -41.66) * mm, "end": v(10.34, -41.28) * mm});
            skArc(sketch, "E40.14.0", {"start": v(10.34, -41.28) * mm, "mid": v(10.34, -40.93) * mm, "end": v(10.32, -40.58) * mm});
            skLineSegment(sketch, "E40.14.1", {"start": v(10.32, -40.58) * mm, "end": v(7.86, -40.82) * mm});
            skArc(sketch, "E40.14.2", {"start": v(7.86, -40.82) * mm, "mid": v(7.75, -39.89) * mm, "end": v(7.53, -38.98) * mm});
            skLineSegment(sketch, "E40.14.3", {"start": v(7.53, -38.98) * mm, "end": v(9.96, -38.47) * mm});
            skArc(sketch, "E40.14.4", {"start": v(9.96, -38.47) * mm, "mid": v(9.85, -38.1) * mm, "end": v(9.72, -37.74) * mm});
            skArc(sketch, "E40.15.0", {"start": v(9.72, -37.74) * mm, "mid": v(9.6, -37.41) * mm, "end": v(9.46, -37.09) * mm});
            skLineSegment(sketch, "E40.15.1", {"start": v(9.46, -37.09) * mm, "end": v(7.23, -38.16) * mm});
            skArc(sketch, "E40.15.2", {"start": v(7.23, -38.16) * mm, "mid": v(6.81, -37.32) * mm, "end": v(6.3, -36.54) * mm});
            skLineSegment(sketch, "E40.15.3", {"start": v(6.3, -36.54) * mm, "end": v(8.4, -35.24) * mm});
            skArc(sketch, "E40.15.4", {"start": v(8.4, -35.24) * mm, "mid": v(8.17, -34.93) * mm, "end": v(7.92, -34.63) * mm});
            skArc(sketch, "E40.16.0", {"start": v(7.92, -34.63) * mm, "mid": v(7.7, -34.36) * mm, "end": v(7.46, -34.1) * mm});
            skLineSegment(sketch, "E40.16.1", {"start": v(7.46, -34.1) * mm, "end": v(5.73, -35.87) * mm});
            skArc(sketch, "E40.16.2", {"start": v(5.73, -35.87) * mm, "mid": v(5.05, -35.23) * mm, "end": v(4.3, -34.67) * mm});
            skLineSegment(sketch, "E40.16.3", {"start": v(4.3, -34.67) * mm, "end": v(5.83, -32.73) * mm});
            skArc(sketch, "E40.16.4", {"start": v(5.83, -32.73) * mm, "mid": v(5.5, -32.52) * mm, "end": v(5.17, -32.32) * mm});
            skArc(sketch, "E40.17.0", {"start": v(5.17, -32.32) * mm, "mid": v(4.87, -32.15) * mm, "end": v(4.56, -31.99) * mm});
            skLineSegment(sketch, "E40.17.1", {"start": v(4.56, -31.99) * mm, "end": v(3.54, -34.24) * mm});
            skArc(sketch, "E40.17.2", {"start": v(3.54, -34.24) * mm, "mid": v(2.68, -33.87) * mm, "end": v(1.78, -33.6) * mm});
            skLineSegment(sketch, "E40.17.3", {"start": v(1.78, -33.6) * mm, "end": v(2.55, -31.25) * mm});
            skArc(sketch, "E40.17.4", {"start": v(2.55, -31.25) * mm, "mid": v(2.18, -31.16) * mm, "end": v(1.8, -31.09) * mm});
            skSolve(sketch);
        }
        {
            var Q0;
            Q0 = qSketchRegion(id + "F7", true);
            extrude(context, id + "F8", {"entities" : qUnion([Q0]), "depth" : 6.35 * mm});
        }
        {
            var Q0;
            Q0=makeQuery(id+"F8.opExtrude","SWEPT_BODY",BODY,{"disambiguationData":[OSD([sQuery(id+"F7.wireOp",EDGE,"E34"),sQuery(id+"F7.wireOp",EDGE,"E35"),sQuery(id+"F7.wireOp",EDGE,"E36"),sQuery(id+"F7.wireOp",EDGE,"E37"),sQuery(id+"F7.wireOp",EDGE,"E38"),sQuery(id+"F7.wireOp",EDGE,"E40.1.0"),sQuery(id+"F7.wireOp",EDGE,"E40.1.1"),sQuery(id+"F7.wireOp",EDGE,"E40.1.2"),sQuery(id+"F7.wireOp",EDGE,"E40.1.3"),sQuery(id+"F7.wireOp",EDGE,"E40.1.4"),sQuery(id+"F7.wireOp",EDGE,"E40.2.0"),sQuery(id+"F7.wireOp",EDGE,"E40.2.1"),sQuery(id+"F7.wireOp",EDGE,"E40.2.2"),sQuery(id+"F7.wireOp",EDGE,"E40.2.3"),sQuery(id+"F7.wireOp",EDGE,"E40.2.4"),sQuery(id+"F7.wireOp",EDGE,"E40.3.0"),sQuery(id+"F7.wireOp",EDGE,"E40.3.1"),sQuery(id+"F7.wireOp",EDGE,"E40.3.2"),sQuery(id+"F7.wireOp",EDGE,"E40.3.3"),sQuery(id+"F7.wireOp",EDGE,"E40.3.4"),sQuery(id+"F7.wireOp",EDGE,"E40.4.0"),sQuery(id+"F7.wireOp",EDGE,"E40.4.1"),sQuery(id+"F7.wireOp",EDGE,"E40.4.2"),sQuery(id+"F7.wireOp",EDGE,"E40.4.3"),sQuery(id+"F7.wireOp",EDGE,"E40.4.4"),sQuery(id+"F7.wireOp",EDGE,"E40.5.0"),sQuery(id+"F7.wireOp",EDGE,"E40.5.1"),sQuery(id+"F7.wireOp",EDGE,"E40.5.2"),sQuery(id+"F7.wireOp",EDGE,"E40.5.3"),sQuery(id+"F7.wireOp",EDGE,"E40.5.4"),sQuery(id+"F7.wireOp",EDGE,"E40.6.0"),sQuery(id+"F7.wireOp",EDGE,"E40.6.1"),sQuery(id+"F7.wireOp",EDGE,"E40.6.2"),sQuery(id+"F7.wireOp",EDGE,"E40.6.3"),sQuery(id+"F7.wireOp",EDGE,"E40.6.4"),sQuery(id+"F7.wireOp",EDGE,"E40.7.0"),sQuery(id+"F7.wireOp",EDGE,"E40.7.1"),sQuery(id+"F7.wireOp",EDGE,"E40.7.2"),sQuery(id+"F7.wireOp",EDGE,"E40.7.3"),sQuery(id+"F7.wireOp",EDGE,"E40.7.4"),sQuery(id+"F7.wireOp",EDGE,"E40.8.0"),sQuery(id+"F7.wireOp",EDGE,"E40.8.1"),sQuery(id+"F7.wireOp",EDGE,"E40.8.2"),sQuery(id+"F7.wireOp",EDGE,"E40.8.3"),sQuery(id+"F7.wireOp",EDGE,"E40.8.4"),sQuery(id+"F7.wireOp",EDGE,"E40.9.0"),sQuery(id+"F7.wireOp",EDGE,"E40.9.1"),sQuery(id+"F7.wireOp",EDGE,"E40.9.2"),sQuery(id+"F7.wireOp",EDGE,"E40.9.3"),sQuery(id+"F7.wireOp",EDGE,"E40.9.4"),sQuery(id+"F7.wireOp",EDGE,"E40.10.0"),sQuery(id+"F7.wireOp",EDGE,"E40.10.1"),sQuery(id+"F7.wireOp",EDGE,"E40.10.2"),sQuery(id+"F7.wireOp",EDGE,"E40.10.3"),sQuery(id+"F7.wireOp",EDGE,"E40.10.4"),sQuery(id+"F7.wireOp",EDGE,"E40.11.0"),sQuery(id+"F7.wireOp",EDGE,"E40.11.1"),sQuery(id+"F7.wireOp",EDGE,"E40.11.2"),sQuery(id+"F7.wireOp",EDGE,"E40.11.3"),sQuery(id+"F7.wireOp",EDGE,"E40.11.4"),sQuery(id+"F7.wireOp",EDGE,"E40.12.0"),sQuery(id+"F7.wireOp",EDGE,"E40.12.1"),sQuery(id+"F7.wireOp",EDGE,"E40.12.2"),sQuery(id+"F7.wireOp",EDGE,"E40.12.3"),sQuery(id+"F7.wireOp",EDGE,"E40.12.4"),sQuery(id+"F7.wireOp",EDGE,"E40.13.0"),sQuery(id+"F7.wireOp",EDGE,"E40.13.1"),sQuery(id+"F7.wireOp",EDGE,"E40.13.2"),sQuery(id+"F7.wireOp",EDGE,"E40.13.3"),sQuery(id+"F7.wireOp",EDGE,"E40.13.4"),sQuery(id+"F7.wireOp",EDGE,"E40.14.0"),sQuery(id+"F7.wireOp",EDGE,"E40.14.1"),sQuery(id+"F7.wireOp",EDGE,"E40.14.2"),sQuery(id+"F7.wireOp",EDGE,"E40.14.3"),sQuery(id+"F7.wireOp",EDGE,"E40.14.4"),sQuery(id+"F7.wireOp",EDGE,"E40.15.0"),sQuery(id+"F7.wireOp",EDGE,"E40.15.1"),sQuery(id+"F7.wireOp",EDGE,"E40.15.2"),sQuery(id+"F7.wireOp",EDGE,"E40.15.3"),sQuery(id+"F7.wireOp",EDGE,"E40.15.4"),sQuery(id+"F7.wireOp",EDGE,"E40.16.0"),sQuery(id+"F7.wireOp",EDGE,"E40.16.1"),sQuery(id+"F7.wireOp",EDGE,"E40.16.2"),sQuery(id+"F7.wireOp",EDGE,"E40.16.3"),sQuery(id+"F7.wireOp",EDGE,"E40.16.4"),sQuery(id+"F7.wireOp",EDGE,"E40.17.0"),sQuery(id+"F7.wireOp",EDGE,"E40.17.1"),sQuery(id+"F7.wireOp",EDGE,"E40.17.2"),sQuery(id+"F7.wireOp",EDGE,"E40.17.3"),sQuery(id+"F7.wireOp",EDGE,"E40.17.4")])]});
            var Q1;
            Q1=sQuery(id+"F0.wireOp",EDGE,"E0");
            circularPattern(context, id + "F9", {"entities" : qUnion([Q0]), "axis" : qUnion([Q1]), "angle" : 360 * degree, "instanceCount" : 3, "equalSpace" : true});
        }
    });
